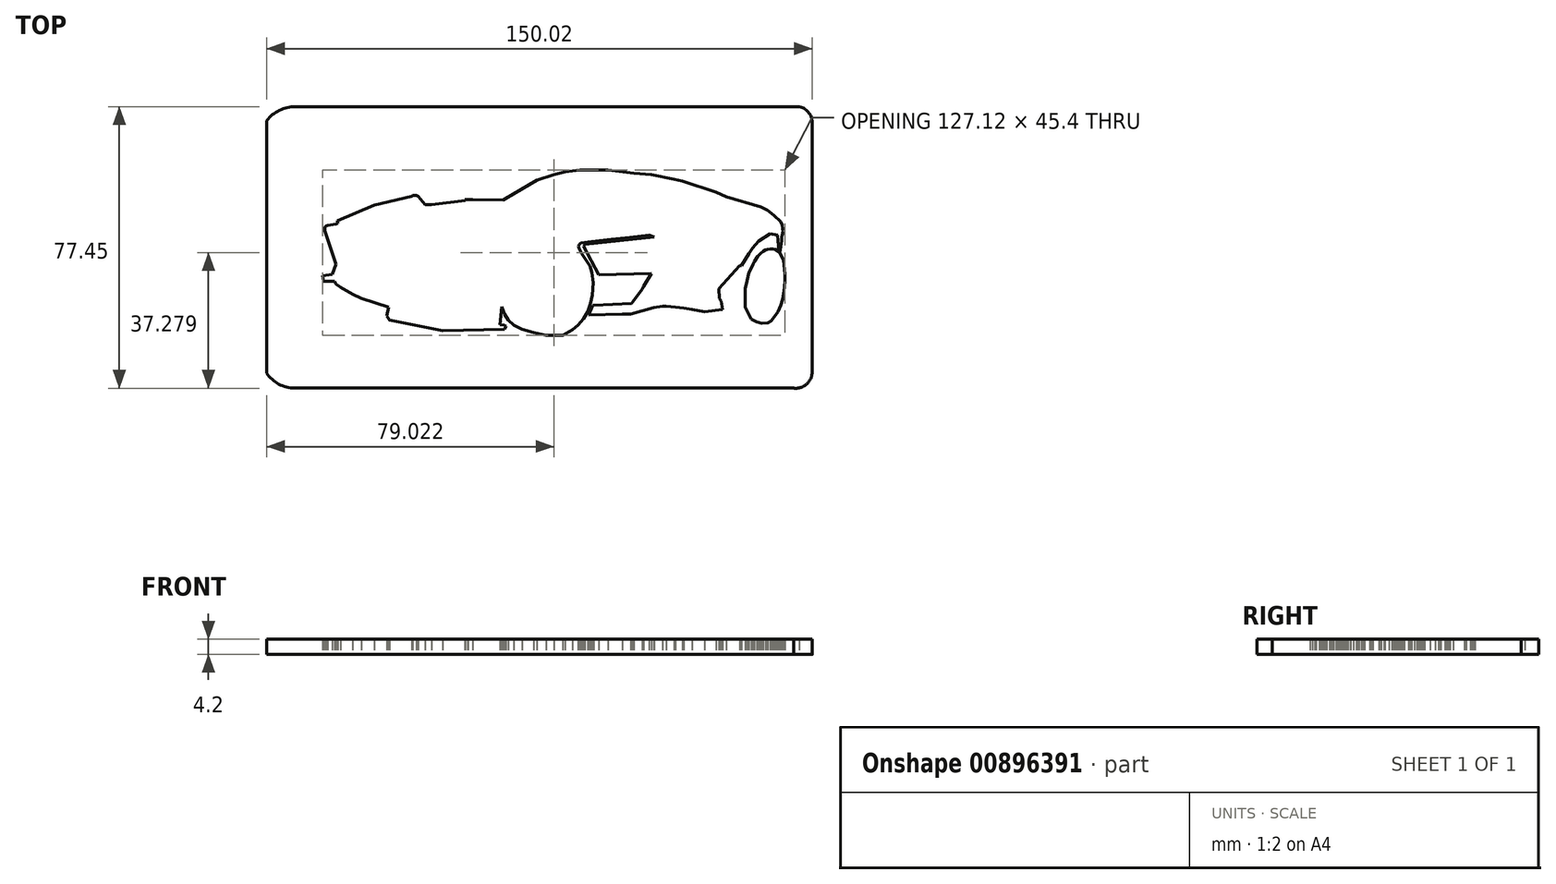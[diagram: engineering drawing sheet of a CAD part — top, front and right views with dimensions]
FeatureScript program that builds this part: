
annotation { "Feature Type Name" : "Feature", "Feature Type Description" : "" }
export const myFeature = defineFeature(function(context is Context, id is Id, definition is map)
    precondition{}
    {
        {
            var Q0;
            Q0=qCreatedBy(makeId("Top.planeOp"),FACE);
            var sketch = newSketch(context, id + "F0", { "sketchPlane" : qUnion([Q0])});
            skLineSegment(sketch, "E0", {"start": v(46.02, 12.97) * mm, "end": v(46.33, 10.6) * mm});
            skLineSegment(sketch, "E1", {"start": v(46.33, 10.6) * mm, "end": v(41.36, 9.95) * mm});
            skLineSegment(sketch, "E2", {"start": v(41.36, 9.95) * mm, "end": v(37.93, 10.6) * mm});
            skLineSegment(sketch, "E3", {"start": v(37.93, 10.6) * mm, "end": v(35.73, 10.96) * mm});
            skLineSegment(sketch, "E4", {"start": v(35.73, 10.96) * mm, "end": v(33.38, 11.3) * mm});
            skLineSegment(sketch, "E5", {"start": v(33.38, 11.3) * mm, "end": v(30.83, 11.58) * mm});
            skLineSegment(sketch, "E6", {"start": v(30.83, 11.58) * mm, "end": v(29.85, 11.58) * mm});
            skLineSegment(sketch, "E7", {"start": v(29.85, 11.58) * mm, "end": v(27.45, 11.2) * mm});
            skLineSegment(sketch, "E8", {"start": v(27.45, 11.2) * mm, "end": v(23.97, 10.17) * mm});
            skLineSegment(sketch, "E9", {"start": v(23.97, 10.17) * mm, "end": v(21.11, 9.32) * mm});
            skLineSegment(sketch, "E10", {"start": v(21.11, 9.32) * mm, "end": v(18.74, 9.32) * mm});
            skLineSegment(sketch, "E11", {"start": v(18.74, 9.32) * mm, "end": v(9.48, 9.1) * mm});
            skLineSegment(sketch, "E12", {"start": v(17.88, 9.3) * mm, "end": v(21.5, 10.48) * mm});
            skLineSegment(sketch, "E13", {"start": v(21.5, 10.48) * mm, "end": v(24.88, 11.32) * mm});
            skLineSegment(sketch, "E14", {"start": v(24.88, 11.32) * mm, "end": v(28.43, 12.23) * mm});
            skLineSegment(sketch, "E15", {"start": v(28.43, 12.23) * mm, "end": v(29.17, 12.25) * mm});
            skLineSegment(sketch, "E16", {"start": v(29.17, 12.25) * mm, "end": v(28.65, 11.39) * mm});
            skLineSegment(sketch, "E17", {"start": v(28.65, 11.39) * mm, "end": v(29.17, 12.25) * mm});
            skLineSegment(sketch, "E18", {"start": v(32.87, 12.25) * mm, "end": v(29.17, 12.25) * mm});
            skLineSegment(sketch, "E19", {"start": v(32.87, 12.25) * mm, "end": v(40.8, 12.42) * mm});
            skLineSegment(sketch, "E20", {"start": v(40.8, 12.42) * mm, "end": v(46.02, 12.97) * mm});
            skLineSegment(sketch, "E21", {"start": v(46.02, 12.97) * mm, "end": v(45.52, 13.64) * mm});
            skLineSegment(sketch, "E22", {"start": v(45.52, 13.64) * mm, "end": v(41.32, 13.38) * mm});
            skLineSegment(sketch, "E23", {"start": v(41.32, 13.38) * mm, "end": v(31.91, 13.38) * mm});
            skLineSegment(sketch, "E24", {"start": v(31.91, 13.38) * mm, "end": v(28.26, 13) * mm});
            skLineSegment(sketch, "E25", {"start": v(28.26, 13) * mm, "end": v(21.76, 12.85) * mm});
            skLineSegment(sketch, "E26", {"start": v(21.76, 12.85) * mm, "end": v(21.38, 12.23) * mm});
            skLineSegment(sketch, "E27", {"start": v(21.38, 12.23) * mm, "end": v(21.7, 11.82) * mm});
            skLineSegment(sketch, "E28", {"start": v(21.7, 11.82) * mm, "end": v(28.43, 12.23) * mm});
            skLineSegment(sketch, "E29", {"start": v(21.7, 11.82) * mm, "end": v(21.93, 11.15) * mm});
            skLineSegment(sketch, "E30", {"start": v(21.93, 11.15) * mm, "end": v(13.63, 10.86) * mm});
            skLineSegment(sketch, "E31", {"start": v(13.63, 10.86) * mm, "end": v(10.15, 10.65) * mm});
            skLineSegment(sketch, "E32", {"start": v(10.15, 10.65) * mm, "end": v(9.48, 9.1) * mm});
            skLineSegment(sketch, "E33", {"start": v(10.15, 10.65) * mm, "end": v(10.66, 11.82) * mm});
            skLineSegment(sketch, "E34", {"start": v(10.9, 11.82) * mm, "end": v(21.38, 12.23) * mm});
            skLineSegment(sketch, "E35", {"start": v(21.76, 12.85) * mm, "end": v(24.3, 16.21) * mm});
            skLineSegment(sketch, "E36", {"start": v(24.3, 16.21) * mm, "end": v(38.2, 18.23) * mm});
            skLineSegment(sketch, "E37", {"start": v(38.2, 18.23) * mm, "end": v(43.88, 22) * mm});
            skLineSegment(sketch, "E38", {"start": v(43.88, 22) * mm, "end": v(42.33, 23.24) * mm});
            skLineSegment(sketch, "E39", {"start": v(42.33, 23.24) * mm, "end": v(47.12, 23.24) * mm});
            skLineSegment(sketch, "E40", {"start": v(47.12, 23.24) * mm, "end": v(49.9, 22.62) * mm});
            skLineSegment(sketch, "E41", {"start": v(49.9, 22.62) * mm, "end": v(43.88, 22) * mm});
            skLineSegment(sketch, "E42", {"start": v(49.9, 22.62) * mm, "end": v(44.7, 16.76) * mm});
            skLineSegment(sketch, "E43", {"start": v(44.7, 16.76) * mm, "end": v(44.7, 14.03) * mm});
            skLineSegment(sketch, "E44", {"start": v(44.7, 14.03) * mm, "end": v(44.98, 13.61) * mm});
            skLineSegment(sketch, "E45", {"start": v(44.98, 13.61) * mm, "end": v(45.52, 13.64) * mm});
            skLineSegment(sketch, "E46", {"start": v(45.52, 13.64) * mm, "end": v(45.34, 16.38) * mm});
            skLineSegment(sketch, "E47", {"start": v(45.34, 16.38) * mm, "end": v(51.01, 22.67) * mm});
            skLineSegment(sketch, "E48", {"start": v(51.01, 22.67) * mm, "end": v(51.56, 22.7) * mm});
            skLineSegment(sketch, "E49", {"start": v(51.56, 22.7) * mm, "end": v(51.01, 22.67) * mm});
            skLineSegment(sketch, "E50", {"start": v(51.56, 22.7) * mm, "end": v(53.55, 26.02) * mm});
            skLineSegment(sketch, "E51", {"start": v(53.55, 26.02) * mm, "end": v(54.56, 27.48) * mm});
            skLineSegment(sketch, "E52", {"start": v(54.56, 27.48) * mm, "end": v(56.31, 29.42) * mm});
            skLineSegment(sketch, "E53", {"start": v(56.31, 29.42) * mm, "end": v(57.68, 30.33) * mm});
            skLineSegment(sketch, "E54", {"start": v(57.68, 30.33) * mm, "end": v(59.45, 31.5) * mm});
            skLineSegment(sketch, "E55", {"start": v(59.45, 31.5) * mm, "end": v(61.43, 31.05) * mm});
            skLineSegment(sketch, "E56", {"start": v(61.43, 31.05) * mm, "end": v(61.89, 26.5) * mm});
            skLineSegment(sketch, "E57", {"start": v(61.89, 26.5) * mm, "end": v(62.16, 26.26) * mm});
            skLineSegment(sketch, "E58", {"start": v(62.16, 26.26) * mm, "end": v(62.56, 29.5) * mm});
            skLineSegment(sketch, "E59", {"start": v(62.56, 29.5) * mm, "end": v(62.56, 30.7) * mm});
            skLineSegment(sketch, "E60", {"start": v(62.56, 30.7) * mm, "end": v(62.76, 30.92) * mm});
            skLineSegment(sketch, "E61", {"start": v(62.76, 30.92) * mm, "end": v(62.88, 31.47) * mm});
            skLineSegment(sketch, "E62", {"start": v(62.88, 31.47) * mm, "end": v(63.06, 32.25) * mm});
            skLineSegment(sketch, "E63", {"start": v(63.06, 32.25) * mm, "end": v(62.88, 32.9) * mm});
            skLineSegment(sketch, "E64", {"start": v(62.88, 32.9) * mm, "end": v(62.74, 33.85) * mm});
            skLineSegment(sketch, "E65", {"start": v(62.74, 33.85) * mm, "end": v(62.4, 34.82) * mm});
            skLineSegment(sketch, "E66", {"start": v(62.4, 34.82) * mm, "end": v(60.48, 36.55) * mm});
            skLineSegment(sketch, "E67", {"start": v(60.48, 36.55) * mm, "end": v(57.7, 36.88) * mm});
            skLineSegment(sketch, "E68", {"start": v(57.7, 36.88) * mm, "end": v(56.06, 36.64) * mm});
            skLineSegment(sketch, "E69", {"start": v(56.06, 36.64) * mm, "end": v(53.85, 35.63) * mm});
            skLineSegment(sketch, "E70", {"start": v(53.85, 35.63) * mm, "end": v(49.63, 33.21) * mm});
            skLineSegment(sketch, "E71", {"start": v(49.63, 33.21) * mm, "end": v(47.78, 32.6) * mm});
            skLineSegment(sketch, "E72", {"start": v(47.78, 32.6) * mm, "end": v(44.93, 31.94) * mm});
            skLineSegment(sketch, "E73", {"start": v(44.93, 31.94) * mm, "end": v(43.07, 31.67) * mm});
            skLineSegment(sketch, "E74", {"start": v(43.07, 31.67) * mm, "end": v(39.45, 31.67) * mm});
            skLineSegment(sketch, "E75", {"start": v(39.45, 31.67) * mm, "end": v(35.8, 32.26) * mm});
            skLineSegment(sketch, "E76", {"start": v(35.8, 32.26) * mm, "end": v(35.02, 32.15) * mm});
            skLineSegment(sketch, "E77", {"start": v(35.02, 32.15) * mm, "end": v(35.43, 31.78) * mm});
            skLineSegment(sketch, "E78", {"start": v(35.43, 31.78) * mm, "end": v(34.34, 31.05) * mm});
            skLineSegment(sketch, "E79", {"start": v(34.34, 31.05) * mm, "end": v(36.34, 29.93) * mm});
            skLineSegment(sketch, "E80", {"start": v(36.34, 29.93) * mm, "end": v(37.89, 28.53) * mm});
            skLineSegment(sketch, "E81", {"start": v(37.89, 28.53) * mm, "end": v(39.87, 26.75) * mm});
            skLineSegment(sketch, "E82", {"start": v(39.87, 26.75) * mm, "end": v(42.33, 23.24) * mm});
            skLineSegment(sketch, "E83", {"start": v(47.12, 23.24) * mm, "end": v(49.28, 26.26) * mm});
            skLineSegment(sketch, "E84", {"start": v(49.28, 26.26) * mm, "end": v(52.77, 30.14) * mm});
            skLineSegment(sketch, "E85", {"start": v(52.77, 30.14) * mm, "end": v(55.72, 32.9) * mm});
            skLineSegment(sketch, "E86", {"start": v(55.72, 32.9) * mm, "end": v(57.45, 34.05) * mm});
            skLineSegment(sketch, "E87", {"start": v(57.45, 34.05) * mm, "end": v(58.82, 34.25) * mm});
            skLineSegment(sketch, "E88", {"start": v(58.82, 34.25) * mm, "end": v(60.58, 33.85) * mm});
            skLineSegment(sketch, "E89", {"start": v(60.58, 33.85) * mm, "end": v(61.4, 33.29) * mm});
            skLineSegment(sketch, "E90", {"start": v(61.88, 32.5) * mm, "end": v(62.56, 30.7) * mm});
            skLineSegment(sketch, "E91", {"start": v(61.4, 33.29) * mm, "end": v(61.88, 32.5) * mm});
            skLineSegment(sketch, "E92", {"start": v(41.01, 26.8) * mm, "end": v(42.38, 27.92) * mm});
            skLineSegment(sketch, "E93", {"start": v(42.38, 27.92) * mm, "end": v(43.42, 29.13) * mm});
            skLineSegment(sketch, "E94", {"start": v(43.42, 29.13) * mm, "end": v(44.8, 30.3) * mm});
            skLineSegment(sketch, "E95", {"start": v(24.3, 16.21) * mm, "end": v(24.83, 16.95) * mm});
            skLineSegment(sketch, "E96", {"start": v(24.83, 16.95) * mm, "end": v(27.35, 17.42) * mm});
            skLineSegment(sketch, "E97", {"start": v(27.35, 17.42) * mm, "end": v(28.1, 17.53) * mm});
            skLineSegment(sketch, "E98", {"start": v(28.1, 17.53) * mm, "end": v(28.43, 17.58) * mm});
            skLineSegment(sketch, "E99", {"start": v(28.43, 17.58) * mm, "end": v(37, 18.72) * mm});
            skLineSegment(sketch, "E100", {"start": v(37, 18.72) * mm, "end": v(34.58, 21.2) * mm});
            skLineSegment(sketch, "E101", {"start": v(34.58, 21.2) * mm, "end": v(34.24, 21.16) * mm});
            skLineSegment(sketch, "E102", {"start": v(34.24, 21.16) * mm, "end": v(26.6, 20.2) * mm});
            skLineSegment(sketch, "E103", {"start": v(26.6, 20.2) * mm, "end": v(24.65, 16.95) * mm});
            skLineSegment(sketch, "E104", {"start": v(24.65, 16.95) * mm, "end": v(24.3, 16.21) * mm});
            skLineSegment(sketch, "E105", {"start": v(24.83, 16.95) * mm, "end": v(24.65, 16.95) * mm});
            skLineSegment(sketch, "E106", {"start": v(25.36, 17.89) * mm, "end": v(36.32, 19.41) * mm});
            skLineSegment(sketch, "E107", {"start": v(35.79, 19.96) * mm, "end": v(25.75, 18.77) * mm});
            skLineSegment(sketch, "E108", {"start": v(25.36, 17.89) * mm, "end": v(25.22, 17.89) * mm});
            skLineSegment(sketch, "E109", {"start": v(26.1, 19.37) * mm, "end": v(35.19, 20.58) * mm});
            skLineSegment(sketch, "E110", {"start": v(34.58, 21.2) * mm, "end": v(37.15, 22.86) * mm});
            skLineSegment(sketch, "E111", {"start": v(35.19, 20.58) * mm, "end": v(38.93, 22.8) * mm});
            skLineSegment(sketch, "E112", {"start": v(35.79, 19.96) * mm, "end": v(40.07, 22.47) * mm});
            skLineSegment(sketch, "E113", {"start": v(36.32, 19.41) * mm, "end": v(39.35, 21.2) * mm});
            skLineSegment(sketch, "E114", {"start": v(37, 18.72) * mm, "end": v(41.95, 22.94) * mm});
            skLineSegment(sketch, "E115", {"start": v(41.95, 22.94) * mm, "end": v(39.54, 26.32) * mm});
            skLineSegment(sketch, "E116", {"start": v(39.54, 26.32) * mm, "end": v(38.05, 28.08) * mm});
            skLineSegment(sketch, "E117", {"start": v(38.05, 28.08) * mm, "end": v(35.94, 29.68) * mm});
            skLineSegment(sketch, "E118", {"start": v(35.94, 29.68) * mm, "end": v(33.28, 30.2) * mm});
            skLineSegment(sketch, "E119", {"start": v(33.28, 30.2) * mm, "end": v(32.31, 30.02) * mm});
            skLineSegment(sketch, "E120", {"start": v(32.31, 30.02) * mm, "end": v(31.77, 29.66) * mm});
            skLineSegment(sketch, "E121", {"start": v(31.77, 29.66) * mm, "end": v(32.15, 29.03) * mm});
            skLineSegment(sketch, "E122", {"start": v(32.15, 29.03) * mm, "end": v(33.31, 27.64) * mm});
            skLineSegment(sketch, "E123", {"start": v(33.31, 27.64) * mm, "end": v(34.28, 26.17) * mm});
            skLineSegment(sketch, "E124", {"start": v(34.28, 26.17) * mm, "end": v(36.03, 24.08) * mm});
            skLineSegment(sketch, "E125", {"start": v(36.03, 24.08) * mm, "end": v(36.1, 23.96) * mm});
            skLineSegment(sketch, "E126", {"start": v(36.1, 23.96) * mm, "end": v(37.15, 22.86) * mm});
            skLineSegment(sketch, "E127", {"start": v(37.15, 22.86) * mm, "end": v(38.93, 23.91) * mm});
            skLineSegment(sketch, "E128", {"start": v(27.56, 24.66) * mm, "end": v(34.58, 21.2) * mm});
            skLineSegment(sketch, "E129", {"start": v(26.6, 20.2) * mm, "end": v(26.83, 20.58) * mm});
            skLineSegment(sketch, "E130", {"start": v(26.83, 20.58) * mm, "end": v(27.92, 30.03) * mm});
            skLineSegment(sketch, "E131", {"start": v(27.92, 30.03) * mm, "end": v(27.56, 30.59) * mm});
            skLineSegment(sketch, "E132", {"start": v(27.56, 30.59) * mm, "end": v(8.52, 28.58) * mm});
            skLineSegment(sketch, "E133", {"start": v(8.52, 28.58) * mm, "end": v(8.12, 28.06) * mm});
            skLineSegment(sketch, "E134", {"start": v(8.12, 28.06) * mm, "end": v(12.32, 20.1) * mm});
            skLineSegment(sketch, "E135", {"start": v(12.32, 20.1) * mm, "end": v(26.83, 20.58) * mm});
            skLineSegment(sketch, "E136", {"start": v(10.9, 11.82) * mm, "end": v(10.66, 11.82) * mm});
            skLineSegment(sketch, "E137", {"start": v(10.64, 11.82) * mm, "end": v(11.7, 15.8) * mm});
            skLineSegment(sketch, "E138", {"start": v(11.7, 15.8) * mm, "end": v(12.32, 20.1) * mm});
            skLineSegment(sketch, "E139", {"start": v(11.25, 27.9) * mm, "end": v(10.75, 26.73) * mm});
            skLineSegment(sketch, "E140", {"start": v(10.75, 26.73) * mm, "end": v(11.49, 26.02) * mm});
            skLineSegment(sketch, "E141", {"start": v(11.49, 26.02) * mm, "end": v(21.03, 27.43) * mm});
            skLineSegment(sketch, "E142", {"start": v(21.03, 27.43) * mm, "end": v(21.7, 28.48) * mm});
            skLineSegment(sketch, "E143", {"start": v(21.7, 28.48) * mm, "end": v(11.25, 27.9) * mm});
            skLineSegment(sketch, "E144", {"start": v(11.25, 27.9) * mm, "end": v(11.06, 27.99) * mm});
            skLineSegment(sketch, "E145", {"start": v(11.06, 27.99) * mm, "end": v(10.27, 26.58) * mm});
            skLineSegment(sketch, "E146", {"start": v(10.27, 26.58) * mm, "end": v(11.43, 25.77) * mm});
            skLineSegment(sketch, "E147", {"start": v(11.43, 25.77) * mm, "end": v(11.49, 26.02) * mm});
            skLineSegment(sketch, "E148", {"start": v(11.43, 25.77) * mm, "end": v(17.72, 26.94) * mm});
            skLineSegment(sketch, "E149", {"start": v(11.06, 27.99) * mm, "end": v(16.78, 28.2) * mm});
            skLineSegment(sketch, "E150", {"start": v(7.66, 25.99) * mm, "end": v(6.92, 27.49) * mm});
            skLineSegment(sketch, "E151", {"start": v(6.92, 27.49) * mm, "end": v(6.8, 27.98) * mm});
            skLineSegment(sketch, "E152", {"start": v(6.8, 27.98) * mm, "end": v(6.96, 28.5) * mm});
            skLineSegment(sketch, "E153", {"start": v(6.96, 28.5) * mm, "end": v(7.36, 28.92) * mm});
            skLineSegment(sketch, "E154", {"start": v(7.36, 28.92) * mm, "end": v(10.36, 29.33) * mm});
            skLineSegment(sketch, "E155", {"start": v(10.36, 29.33) * mm, "end": v(15.7, 29.9) * mm});
            skLineSegment(sketch, "E156", {"start": v(15.7, 29.9) * mm, "end": v(20.77, 30.46) * mm});
            skLineSegment(sketch, "E157", {"start": v(20.77, 30.46) * mm, "end": v(26.13, 31.02) * mm});
            skLineSegment(sketch, "E158", {"start": v(26.13, 31.02) * mm, "end": v(27.56, 30.59) * mm});
            skLineSegment(sketch, "E159", {"start": v(10.66, 11.82) * mm, "end": v(9.97, 11.82) * mm});
            skLineSegment(sketch, "E160", {"start": v(15.7, 29.9) * mm, "end": v(15.33, 30.17) * mm});
            skLineSegment(sketch, "E161", {"start": v(15.33, 30.54) * mm, "end": v(15.33, 30.17) * mm});
            skLineSegment(sketch, "E162", {"start": v(15.33, 30.54) * mm, "end": v(15.06, 30.7) * mm});
            skLineSegment(sketch, "E163", {"start": v(15.06, 30.7) * mm, "end": v(14.87, 31.08) * mm});
            skLineSegment(sketch, "E164", {"start": v(14.87, 31.08) * mm, "end": v(14.5, 31.04) * mm});
            skLineSegment(sketch, "E165", {"start": v(14.5, 31.04) * mm, "end": v(14.3, 30.94) * mm});
            skLineSegment(sketch, "E166", {"start": v(14.3, 30.94) * mm, "end": v(8.21, 29.9) * mm});
            skLineSegment(sketch, "E167", {"start": v(13.1, 30.74) * mm, "end": v(12.9, 31.1) * mm});
            skLineSegment(sketch, "E168", {"start": v(12.9, 31.1) * mm, "end": v(12.9, 32.83) * mm});
            skLineSegment(sketch, "E169", {"start": v(12.9, 32.83) * mm, "end": v(12.53, 33.2) * mm});
            skLineSegment(sketch, "E170", {"start": v(12.53, 33.2) * mm, "end": v(4.45, 31.8) * mm});
            skLineSegment(sketch, "E171", {"start": v(4.45, 31.8) * mm, "end": v(7.43, 29.44) * mm});
            skLineSegment(sketch, "E172", {"start": v(7.43, 29.44) * mm, "end": v(6.8, 29.01) * mm});
            skLineSegment(sketch, "E173", {"start": v(6.8, 29.01) * mm, "end": v(6.33, 28.35) * mm});
            skLineSegment(sketch, "E174", {"start": v(6.33, 28.35) * mm, "end": v(6.33, 27.84) * mm});
            skLineSegment(sketch, "E175", {"start": v(6.33, 27.84) * mm, "end": v(6.57, 27.31) * mm});
            skLineSegment(sketch, "E176", {"start": v(6.57, 27.31) * mm, "end": v(7.1, 26.46) * mm});
            skLineSegment(sketch, "E177", {"start": v(7.1, 26.46) * mm, "end": v(7.66, 25.99) * mm});
            skLineSegment(sketch, "E178", {"start": v(15.06, 30.7) * mm, "end": v(11.3, 29.7) * mm});
            skLineSegment(sketch, "E179", {"start": v(12.81, 32.92) * mm, "end": v(7.38, 31.3) * mm});
            skLineSegment(sketch, "E180", {"start": v(7.38, 31.3) * mm, "end": v(12.9, 31.1) * mm});
            skLineSegment(sketch, "E181", {"start": v(6.33, 28.35) * mm, "end": v(5.03, 29.64) * mm});
            skLineSegment(sketch, "E182", {"start": v(5.03, 29.64) * mm, "end": v(4.82, 27.98) * mm});
            skLineSegment(sketch, "E183", {"start": v(5.03, 29.64) * mm, "end": v(2.75, 31.92) * mm});
            skLineSegment(sketch, "E184", {"start": v(2.75, 31.92) * mm, "end": v(2.42, 32.67) * mm});
            skLineSegment(sketch, "E185", {"start": v(2.42, 32.67) * mm, "end": v(2.08, 32.52) * mm});
            skLineSegment(sketch, "E186", {"start": v(2.08, 32.52) * mm, "end": v(1.85, 32.75) * mm});
            skLineSegment(sketch, "E187", {"start": v(1.85, 32.75) * mm, "end": v(1.16, 33.06) * mm});
            skLineSegment(sketch, "E188", {"start": v(1.16, 33.06) * mm, "end": v(-1.02, 33.82) * mm});
            skLineSegment(sketch, "E189", {"start": v(-1.02, 33.82) * mm, "end": v(1.56, 34) * mm});
            skLineSegment(sketch, "E190", {"start": v(1.56, 34) * mm, "end": v(4.45, 31.8) * mm});
            skLineSegment(sketch, "E191", {"start": v(1.56, 34) * mm, "end": v(1.56, 32.88) * mm});
            skLineSegment(sketch, "E192", {"start": v(1.56, 34) * mm, "end": v(1.77, 34.27) * mm});
            skLineSegment(sketch, "E193", {"start": v(1.77, 34.27) * mm, "end": v(7.95, 34.96) * mm});
            skLineSegment(sketch, "E194", {"start": v(7.95, 34.96) * mm, "end": v(10.49, 32.84) * mm});
            skLineSegment(sketch, "E195", {"start": v(2.75, 31.92) * mm, "end": v(2.6, 31.6) * mm});
            skLineSegment(sketch, "E196", {"start": v(2.6, 31.6) * mm, "end": v(3.02, 30.82) * mm});
            skLineSegment(sketch, "E197", {"start": v(3.03, 30.77) * mm, "end": v(1.23, 30.16) * mm});
            skLineSegment(sketch, "E198", {"start": v(1.23, 30.16) * mm, "end": v(1.23, 31.03) * mm});
            skLineSegment(sketch, "E199", {"start": v(1.23, 31.03) * mm, "end": v(1.39, 31.17) * mm});
            skLineSegment(sketch, "E200", {"start": v(1.39, 31.17) * mm, "end": v(2.6, 31.6) * mm});
            skLineSegment(sketch, "E201", {"start": v(2.75, 31.92) * mm, "end": v(1.23, 31.6) * mm});
            skPoint(sketch, "E201.endSnap0", {"position": v(1.23, 30.6) * mm});
            skLineSegment(sketch, "E202", {"start": v(1.23, 31.6) * mm, "end": v(1.09, 31.03) * mm});
            skLineSegment(sketch, "E203", {"start": v(1.09, 31.03) * mm, "end": v(1.09, 30.16) * mm});
            skLineSegment(sketch, "E204", {"start": v(1.09, 30.16) * mm, "end": v(-1.84, 29.3) * mm});
            skLineSegment(sketch, "E205", {"start": v(-1.84, 29.3) * mm, "end": v(-3.52, 28.53) * mm});
            skLineSegment(sketch, "E206", {"start": v(-3.52, 28.53) * mm, "end": v(-4.85, 27.84) * mm});
            skLineSegment(sketch, "E207", {"start": v(-4.85, 27.84) * mm, "end": v(-5.64, 27.19) * mm});
            skLineSegment(sketch, "E208", {"start": v(-5.64, 27.19) * mm, "end": v(-6.73, 26.3) * mm});
            skLineSegment(sketch, "E209", {"start": v(-6.73, 26.3) * mm, "end": v(-5.83, 27.19) * mm});
            skLineSegment(sketch, "E210", {"start": v(-5.83, 27.19) * mm, "end": v(-4.92, 27.92) * mm});
            skLineSegment(sketch, "E211", {"start": v(-4.92, 27.92) * mm, "end": v(-3.65, 28.58) * mm});
            skLineSegment(sketch, "E212", {"start": v(-3.65, 28.58) * mm, "end": v(-1.84, 29.3) * mm});
            skLineSegment(sketch, "E213", {"start": v(1.85, 32.52) * mm, "end": v(0.7, 32.25) * mm});
            skLineSegment(sketch, "E214", {"start": v(0.7, 32.25) * mm, "end": v(0.3, 30.83) * mm});
            skLineSegment(sketch, "E215", {"start": v(0.3, 30.83) * mm, "end": v(-0.13, 30.83) * mm});
            skLineSegment(sketch, "E216", {"start": v(-0.13, 30.83) * mm, "end": v(0.17, 32.05) * mm});
            skLineSegment(sketch, "E217", {"start": v(0.17, 32.05) * mm, "end": v(0.7, 32.25) * mm});
            skLineSegment(sketch, "E218", {"start": v(-0.13, 30.83) * mm, "end": v(-2.4, 30.02) * mm});
            skLineSegment(sketch, "E219", {"start": v(-2.4, 30.02) * mm, "end": v(-4.08, 29.43) * mm});
            skLineSegment(sketch, "E220", {"start": v(-4.08, 29.43) * mm, "end": v(-5.07, 28.98) * mm});
            skLineSegment(sketch, "E221", {"start": v(-5.07, 28.98) * mm, "end": v(-6.76, 27.85) * mm});
            skLineSegment(sketch, "E222", {"start": v(-6.76, 27.85) * mm, "end": v(-7.88, 26.73) * mm});
            skLineSegment(sketch, "E223", {"start": v(-7.88, 26.73) * mm, "end": v(-9.98, 23.95) * mm});
            skLineSegment(sketch, "E224", {"start": v(-9.98, 23.95) * mm, "end": v(-11.7, 21.06) * mm});
            skLineSegment(sketch, "E225", {"start": v(-11.7, 21.06) * mm, "end": v(-14.23, 16.13) * mm});
            skLineSegment(sketch, "E226", {"start": v(-14.23, 16.13) * mm, "end": v(-16.25, 11.5) * mm});
            skLineSegment(sketch, "E227", {"start": v(-16.25, 11.5) * mm, "end": v(-16.25, 11.04) * mm});
            skLineSegment(sketch, "E228", {"start": v(-16.25, 11.04) * mm, "end": v(-14.32, 11.37) * mm});
            skLineSegment(sketch, "E229", {"start": v(-14.32, 11.37) * mm, "end": v(-14.82, 6.38) * mm});
            skLineSegment(sketch, "E230", {"start": v(-14.82, 6.38) * mm, "end": v(-13.63, 6.26) * mm});
            skLineSegment(sketch, "E231", {"start": v(-13.63, 6.26) * mm, "end": v(-13.2, 6.07) * mm});
            skLineSegment(sketch, "E232", {"start": v(-13.2, 6.07) * mm, "end": v(-13.6, 5.14) * mm});
            skLineSegment(sketch, "E233", {"start": v(-13.6, 5.14) * mm, "end": v(-30.55, 4.76) * mm});
            skLineSegment(sketch, "E234", {"start": v(-30.55, 4.76) * mm, "end": v(-31.58, 5.78) * mm});
            skLineSegment(sketch, "E235", {"start": v(-31.07, 5.27) * mm, "end": v(-13.37, 5.66) * mm});
            skLineSegment(sketch, "E236", {"start": v(-14.82, 6.38) * mm, "end": v(-27.36, 6) * mm});
            skLineSegment(sketch, "E237", {"start": v(-27.36, 6) * mm, "end": v(-25.98, 9.2) * mm});
            skLineSegment(sketch, "E238", {"start": v(-25.98, 9.2) * mm, "end": v(-16.25, 11.04) * mm});
            skLineSegment(sketch, "E239", {"start": v(-16.25, 11.5) * mm, "end": v(-26.4, 9.57) * mm});
            skLineSegment(sketch, "E240", {"start": v(-26.4, 9.57) * mm, "end": v(-28.65, 6.38) * mm});
            skLineSegment(sketch, "E241", {"start": v(-28.65, 6.38) * mm, "end": v(-27.36, 6) * mm});
            skLineSegment(sketch, "E242", {"start": v(-28.23, 6.98) * mm, "end": v(-30.43, 6.93) * mm});
            skLineSegment(sketch, "E243", {"start": v(-30.43, 6.93) * mm, "end": v(-31.14, 6.8) * mm});
            skLineSegment(sketch, "E244", {"start": v(-31.14, 6.8) * mm, "end": v(-32.86, 7.3) * mm});
            skLineSegment(sketch, "E245", {"start": v(-30.55, 4.76) * mm, "end": v(-45.21, 7.67) * mm});
            skLineSegment(sketch, "E246", {"start": v(-45.21, 7.67) * mm, "end": v(-45.95, 8.88) * mm});
            skLineSegment(sketch, "E247", {"start": v(-45.95, 8.88) * mm, "end": v(-45.41, 11.24) * mm});
            skLineSegment(sketch, "E248", {"start": v(-45.95, 8.88) * mm, "end": v(-31.58, 5.78) * mm});
            skLineSegment(sketch, "E249", {"start": v(-45.95, 8.88) * mm, "end": v(-42.57, 9.23) * mm});
            skLineSegment(sketch, "E250", {"start": v(-42.57, 9.23) * mm, "end": v(-37.9, 8.16) * mm});
            skLineSegment(sketch, "E251", {"start": v(-37.9, 8.16) * mm, "end": v(-39.32, 7.45) * mm});
            skLineSegment(sketch, "E252", {"start": v(-37.9, 8.16) * mm, "end": v(-36.33, 8.6) * mm});
            skLineSegment(sketch, "E253", {"start": v(-36.33, 8.6) * mm, "end": v(-34.7, 9.35) * mm});
            skLineSegment(sketch, "E254", {"start": v(-34.7, 9.35) * mm, "end": v(-32.06, 11.73) * mm});
            skLineSegment(sketch, "E255", {"start": v(-32.06, 11.73) * mm, "end": v(-31.22, 11.73) * mm});
            skLineSegment(sketch, "E256", {"start": v(-31.22, 11.73) * mm, "end": v(-32.63, 10) * mm});
            skLineSegment(sketch, "E257", {"start": v(-32.63, 10) * mm, "end": v(-33.08, 9.49) * mm});
            skLineSegment(sketch, "E258", {"start": v(-33.08, 9.49) * mm, "end": v(-34.08, 8.85) * mm});
            skLineSegment(sketch, "E259", {"start": v(-34.08, 8.85) * mm, "end": v(-35.85, 7.92) * mm});
            skLineSegment(sketch, "E260", {"start": v(-35.85, 7.92) * mm, "end": v(-36.4, 7.63) * mm});
            skLineSegment(sketch, "E261", {"start": v(-36.4, 7.63) * mm, "end": v(-34.9, 7.63) * mm});
            skLineSegment(sketch, "E262", {"start": v(-34.9, 7.63) * mm, "end": v(-36.83, 7.27) * mm});
            skLineSegment(sketch, "E263", {"start": v(-36.83, 7.27) * mm, "end": v(-34.25, 7.46) * mm});
            skLineSegment(sketch, "E264", {"start": v(-34.25, 7.46) * mm, "end": v(-32.86, 7.3) * mm});
            skLineSegment(sketch, "E265", {"start": v(-31.22, 11.73) * mm, "end": v(-30.18, 11.93) * mm});
            skLineSegment(sketch, "E266", {"start": v(-32.06, 11.73) * mm, "end": v(-44.88, 15.57) * mm});
            skLineSegment(sketch, "E267", {"start": v(-44.88, 15.57) * mm, "end": v(-49.46, 20.72) * mm});
            skLineSegment(sketch, "E268", {"start": v(-49.46, 20.72) * mm, "end": v(-50.22, 20.72) * mm});
            skLineSegment(sketch, "E269", {"start": v(-50.22, 20.72) * mm, "end": v(-50.7, 20.72) * mm});
            skLineSegment(sketch, "E270", {"start": v(-50.7, 20.72) * mm, "end": v(-53.17, 18.65) * mm});
            skLineSegment(sketch, "E271", {"start": v(-50.94, 20.25) * mm, "end": v(-50.54, 20.25) * mm});
            skLineSegment(sketch, "E272", {"start": v(-50.54, 20.25) * mm, "end": v(-51.26, 20.25) * mm});
            skLineSegment(sketch, "E273", {"start": v(-51.26, 20.25) * mm, "end": v(-50.94, 20.25) * mm});
            skLineSegment(sketch, "E274", {"start": v(-50.54, 20.25) * mm, "end": v(-45.9, 15.26) * mm});
            skLineSegment(sketch, "E275", {"start": v(-45.9, 15.26) * mm, "end": v(-32.88, 11) * mm});
            skLineSegment(sketch, "E276", {"start": v(-34.7, 12.52) * mm, "end": v(-44.02, 23.5) * mm});
            skLineSegment(sketch, "E277", {"start": v(-44.02, 23.5) * mm, "end": v(-52.98, 25.26) * mm});
            skLineSegment(sketch, "E278", {"start": v(-52.98, 25.26) * mm, "end": v(-53.91, 27.53) * mm});
            skLineSegment(sketch, "E279", {"start": v(-53.91, 27.53) * mm, "end": v(-58.62, 30.93) * mm});
            skLineSegment(sketch, "E280", {"start": v(-58.62, 30.93) * mm, "end": v(-58.48, 32.14) * mm});
            skLineSegment(sketch, "E281", {"start": v(-58.48, 32.14) * mm, "end": v(-57.8, 32.98) * mm});
            skLineSegment(sketch, "E282", {"start": v(-57.8, 32.98) * mm, "end": v(-59.01, 34.55) * mm});
            skLineSegment(sketch, "E283", {"start": v(-59.01, 34.55) * mm, "end": v(-59.38, 33.32) * mm});
            skLineSegment(sketch, "E284", {"start": v(-59.38, 33.32) * mm, "end": v(-58.48, 32.14) * mm});
            skLineSegment(sketch, "E285", {"start": v(-59.38, 33.32) * mm, "end": v(-59.83, 33.69) * mm});
            skLineSegment(sketch, "E286", {"start": v(-59.83, 33.69) * mm, "end": v(-62.48, 33.32) * mm});
            skLineSegment(sketch, "E287", {"start": v(-59.9, 34.14) * mm, "end": v(-62.17, 33.77) * mm});
            skLineSegment(sketch, "E288", {"start": v(-62.17, 33.77) * mm, "end": v(-62.64, 33.6) * mm});
            skLineSegment(sketch, "E289", {"start": v(-62.64, 33.6) * mm, "end": v(-62.96, 33.34) * mm});
            skLineSegment(sketch, "E290", {"start": v(-62.96, 33.34) * mm, "end": v(-62.96, 32.2) * mm});
            skLineSegment(sketch, "E291", {"start": v(-62.96, 32.2) * mm, "end": v(-59.12, 20.61) * mm});
            skLineSegment(sketch, "E292", {"start": v(-59.12, 20.61) * mm, "end": v(-59.72, 20.28) * mm});
            skLineSegment(sketch, "E293", {"start": v(-59.72, 20.28) * mm, "end": v(-59.88, 20.16) * mm});
            skLineSegment(sketch, "E294", {"start": v(-59.88, 20.16) * mm, "end": v(-60.08, 19.97) * mm});
            skLineSegment(sketch, "E295", {"start": v(-60.08, 19.97) * mm, "end": v(-60.08, 19.13) * mm});
            skLineSegment(sketch, "E296", {"start": v(-60.08, 19.13) * mm, "end": v(-59.3, 18.22) * mm});
            skLineSegment(sketch, "E297", {"start": v(-59.3, 18.22) * mm, "end": v(-55.38, 15.96) * mm});
            skLineSegment(sketch, "E298", {"start": v(-55.38, 15.96) * mm, "end": v(-51.26, 20.25) * mm});
            skLineSegment(sketch, "E299", {"start": v(-54.3, 15.52) * mm, "end": v(-54.3, 15.84) * mm});
            skLineSegment(sketch, "E300", {"start": v(-54.3, 15.84) * mm, "end": v(-52.98, 18.1) * mm});
            skLineSegment(sketch, "E301", {"start": v(-54.3, 15.52) * mm, "end": v(-50.66, 14.06) * mm});
            skLineSegment(sketch, "E302", {"start": v(-50.66, 14.06) * mm, "end": v(-48.28, 13.25) * mm});
            skLineSegment(sketch, "E303", {"start": v(-48.28, 13.25) * mm, "end": v(-44.72, 12.3) * mm});
            skLineSegment(sketch, "E304", {"start": v(-44.72, 12.3) * mm, "end": v(-41.74, 11.77) * mm});
            skLineSegment(sketch, "E305", {"start": v(-41.74, 11.77) * mm, "end": v(-33.2, 10.7) * mm});
            skLineSegment(sketch, "E306", {"start": v(-33.2, 10.7) * mm, "end": v(-34.7, 9.35) * mm});
            skLineSegment(sketch, "E307", {"start": v(-34.55, 9.49) * mm, "end": v(-45.41, 11.24) * mm});
            skLineSegment(sketch, "E308", {"start": v(-45.41, 11.24) * mm, "end": v(-49.32, 12.52) * mm});
            skLineSegment(sketch, "E309", {"start": v(-49.32, 12.52) * mm, "end": v(-52.98, 13.72) * mm});
            skLineSegment(sketch, "E310", {"start": v(-52.98, 13.72) * mm, "end": v(-55.31, 14.77) * mm});
            skLineSegment(sketch, "E311", {"start": v(-55.31, 14.77) * mm, "end": v(-58.64, 16.69) * mm});
            skLineSegment(sketch, "E312", {"start": v(-58.64, 16.69) * mm, "end": v(-59.95, 17.65) * mm});
            skLineSegment(sketch, "E313", {"start": v(-59.95, 17.65) * mm, "end": v(-60.26, 18.33) * mm});
            skLineSegment(sketch, "E314", {"start": v(-60.26, 18.33) * mm, "end": v(-60.34, 18.6) * mm});
            skLineSegment(sketch, "E315", {"start": v(-60.34, 18.6) * mm, "end": v(-60.08, 19.97) * mm});
            skLineSegment(sketch, "E316", {"start": v(-59.12, 20.61) * mm, "end": v(-58.56, 20.8) * mm});
            skLineSegment(sketch, "E317", {"start": v(-58.56, 20.8) * mm, "end": v(-58.06, 20.96) * mm});
            skLineSegment(sketch, "E318", {"start": v(-58.06, 20.96) * mm, "end": v(-57.59, 21.12) * mm});
            skLineSegment(sketch, "E319", {"start": v(-57.59, 21.12) * mm, "end": v(-56.78, 20.78) * mm});
            skLineSegment(sketch, "E320", {"start": v(-56.78, 20.78) * mm, "end": v(-55.5, 19.97) * mm});
            skLineSegment(sketch, "E321", {"start": v(-55.5, 19.97) * mm, "end": v(-53.17, 18.65) * mm});
            skLineSegment(sketch, "E322", {"start": v(-58.56, 20.8) * mm, "end": v(-59.53, 24.4) * mm});
            skLineSegment(sketch, "E323", {"start": v(-59.53, 24.4) * mm, "end": v(-60.34, 29.57) * mm});
            skLineSegment(sketch, "E324", {"start": v(-60.34, 29.57) * mm, "end": v(-60.6, 30.88) * mm});
            skLineSegment(sketch, "E325", {"start": v(-60.6, 30.88) * mm, "end": v(-60.7, 31.16) * mm});
            skLineSegment(sketch, "E326", {"start": v(-60.7, 31.16) * mm, "end": v(-58.94, 31.16) * mm});
            skLineSegment(sketch, "E327", {"start": v(-58.94, 31.16) * mm, "end": v(-58.71, 30.48) * mm});
            skLineSegment(sketch, "E328", {"start": v(-58.71, 30.48) * mm, "end": v(-58.35, 30.48) * mm});
            skLineSegment(sketch, "E329", {"start": v(-58.35, 30.48) * mm, "end": v(-58.35, 30.74) * mm});
            skLineSegment(sketch, "E330", {"start": v(-58.94, 31.16) * mm, "end": v(-58.93, 32.73) * mm});
            skLineSegment(sketch, "E331", {"start": v(-58.35, 30.48) * mm, "end": v(-57.6, 27.8) * mm});
            skLineSegment(sketch, "E332", {"start": v(-57.6, 27.8) * mm, "end": v(-60.6, 30.88) * mm});
            skLineSegment(sketch, "E333", {"start": v(-60.6, 30.88) * mm, "end": v(-58.5, 27.85) * mm});
            skLineSegment(sketch, "E334", {"start": v(-58.5, 27.85) * mm, "end": v(-56.5, 25.79) * mm});
            skLineSegment(sketch, "E335", {"start": v(-56.5, 25.79) * mm, "end": v(-55.69, 21.88) * mm});
            skLineSegment(sketch, "E336", {"start": v(-55.69, 21.88) * mm, "end": v(-56.93, 23.82) * mm});
            skLineSegment(sketch, "E337", {"start": v(-56.93, 23.82) * mm, "end": v(-55.65, 21.43) * mm});
            skLineSegment(sketch, "E338", {"start": v(-55.65, 21.43) * mm, "end": v(-55.5, 21.58) * mm});
            skLineSegment(sketch, "E339", {"start": v(-55.5, 21.58) * mm, "end": v(-55.69, 21.88) * mm});
            skLineSegment(sketch, "E340", {"start": v(-55.99, 22.05) * mm, "end": v(-57.15, 22.05) * mm});
            skLineSegment(sketch, "E341", {"start": v(-57.15, 22.05) * mm, "end": v(-58.03, 21.28) * mm});
            skLineSegment(sketch, "E342", {"start": v(-55.65, 21.43) * mm, "end": v(-52.27, 19.4) * mm});
            skLineSegment(sketch, "E343", {"start": v(-59.9, 34.14) * mm, "end": v(-59.44, 34.43) * mm});
            skLineSegment(sketch, "E344", {"start": v(-59.44, 34.43) * mm, "end": v(-59.44, 34.68) * mm});
            skLineSegment(sketch, "E345", {"start": v(-59.44, 34.68) * mm, "end": v(-59.54, 34.8) * mm});
            skLineSegment(sketch, "E346", {"start": v(-59.54, 34.8) * mm, "end": v(-59.54, 35.02) * mm});
            skLineSegment(sketch, "E347", {"start": v(-59.54, 35.02) * mm, "end": v(-49.35, 39.33) * mm});
            skLineSegment(sketch, "E348", {"start": v(-49.35, 39.33) * mm, "end": v(-39.09, 41.76) * mm});
            skLineSegment(sketch, "E349", {"start": v(-39.09, 41.76) * mm, "end": v(-38.1, 41.76) * mm});
            skLineSegment(sketch, "E350", {"start": v(-38.1, 41.76) * mm, "end": v(-35.9, 39.26) * mm});
            skLineSegment(sketch, "E351", {"start": v(-35.9, 39.26) * mm, "end": v(-33.67, 39.49) * mm});
            skLineSegment(sketch, "E352", {"start": v(-33.67, 39.49) * mm, "end": v(-35.37, 39.49) * mm});
            skLineSegment(sketch, "E353", {"start": v(-35.37, 39.49) * mm, "end": v(-37.33, 41.78) * mm});
            skLineSegment(sketch, "E354", {"start": v(-37.33, 41.78) * mm, "end": v(-37.84, 42) * mm});
            skLineSegment(sketch, "E355", {"start": v(-37.84, 42) * mm, "end": v(-38.86, 42) * mm});
            skLineSegment(sketch, "E356", {"start": v(-39.09, 41.76) * mm, "end": v(-38.86, 42) * mm});
            skLineSegment(sketch, "E357", {"start": v(-33.67, 39.49) * mm, "end": v(-24.42, 40.6) * mm});
            skLineSegment(sketch, "E358", {"start": v(-24.42, 40.6) * mm, "end": v(-24.45, 40.82) * mm});
            skLineSegment(sketch, "E359", {"start": v(-24.45, 40.82) * mm, "end": v(-23.78, 40.9) * mm});
            skLineSegment(sketch, "E360", {"start": v(-23.78, 40.9) * mm, "end": v(-22.17, 40.24) * mm});
            skLineSegment(sketch, "E361", {"start": v(-22.17, 40.24) * mm, "end": v(-20.75, 40.24) * mm});
            skLineSegment(sketch, "E362", {"start": v(-20.75, 40.24) * mm, "end": v(-22.29, 40.86) * mm});
            skLineSegment(sketch, "E363", {"start": v(-22.29, 40.86) * mm, "end": v(-23.68, 40.86) * mm});
            skLineSegment(sketch, "E364", {"start": v(-24.42, 40.6) * mm, "end": v(-22.45, 39.94) * mm});
            skLineSegment(sketch, "E365", {"start": v(-22.45, 39.94) * mm, "end": v(-22.45, 39.6) * mm});
            skLineSegment(sketch, "E366", {"start": v(-22.45, 39.6) * mm, "end": v(-24.42, 39.26) * mm});
            skLineSegment(sketch, "E367", {"start": v(-24.42, 39.26) * mm, "end": v(-26.8, 38.76) * mm});
            skLineSegment(sketch, "E368", {"start": v(-26.8, 38.76) * mm, "end": v(-29.2, 38.22) * mm});
            skLineSegment(sketch, "E369", {"start": v(-29.2, 38.22) * mm, "end": v(-31.1, 37.68) * mm});
            skLineSegment(sketch, "E370", {"start": v(-31.1, 37.68) * mm, "end": v(-33.95, 36.81) * mm});
            skLineSegment(sketch, "E371", {"start": v(-33.95, 36.81) * mm, "end": v(-36.12, 35.8) * mm});
            skLineSegment(sketch, "E372", {"start": v(-36.12, 35.8) * mm, "end": v(-32.15, 34.67) * mm});
            skLineSegment(sketch, "E373", {"start": v(-32.15, 34.67) * mm, "end": v(-28.75, 35.43) * mm});
            skLineSegment(sketch, "E374", {"start": v(-28.75, 35.43) * mm, "end": v(-33.6, 36.61) * mm});
            skLineSegment(sketch, "E375", {"start": v(-33.6, 36.61) * mm, "end": v(-32.04, 37.4) * mm});
            skLineSegment(sketch, "E376", {"start": v(-31.67, 36.15) * mm, "end": v(-27.94, 37.64) * mm});
            skLineSegment(sketch, "E377", {"start": v(-27.94, 37.64) * mm, "end": v(-24.2, 36.72) * mm});
            skLineSegment(sketch, "E378", {"start": v(-28.75, 35.43) * mm, "end": v(-24.2, 36.72) * mm});
            skLineSegment(sketch, "E379", {"start": v(-25.67, 37.08) * mm, "end": v(-26.07, 37.42) * mm});
            skPoint(sketch, "E379.endSnap0", {"position": v(-26.07, 37.18) * mm});
            skLineSegment(sketch, "E380", {"start": v(-26.07, 37.42) * mm, "end": v(-21.82, 38.8) * mm});
            skLineSegment(sketch, "E381", {"start": v(-53.91, 27.53) * mm, "end": v(-42.73, 25.51) * mm});
            skLineSegment(sketch, "E382", {"start": v(-42.73, 25.51) * mm, "end": v(-42.5, 26.75) * mm});
            skLineSegment(sketch, "E383", {"start": v(-42.5, 26.75) * mm, "end": v(-39.29, 27.15) * mm});
            skLineSegment(sketch, "E384", {"start": v(-39.29, 27.15) * mm, "end": v(-39.29, 25.65) * mm});
            skLineSegment(sketch, "E385", {"start": v(-39.29, 25.65) * mm, "end": v(-42.73, 25.51) * mm});
            skLineSegment(sketch, "E386", {"start": v(-39.29, 27.15) * mm, "end": v(-28.12, 25.51) * mm});
            skLineSegment(sketch, "E387", {"start": v(-28.12, 25.51) * mm, "end": v(-10.87, 26.92) * mm});
            skLineSegment(sketch, "E388", {"start": v(-10.87, 26.92) * mm, "end": v(0.17, 32.05) * mm});
            skLineSegment(sketch, "E389", {"start": v(-20.96, 26.1) * mm, "end": v(-15.8, 27.8) * mm});
            skLineSegment(sketch, "E390", {"start": v(-25.93, 26.66) * mm, "end": v(-13.65, 30.43) * mm});
            skPoint(sketch, "E390.endSnap0", {"position": v(-1.26, 30.43) * mm});
            skLineSegment(sketch, "E391", {"start": v(-13.65, 30.43) * mm, "end": v(-17.22, 30.8) * mm});
            skLineSegment(sketch, "E392", {"start": v(-17.22, 30.8) * mm, "end": v(-22.72, 28.98) * mm});
            skLineSegment(sketch, "E393", {"start": v(-22.72, 28.98) * mm, "end": v(-25.86, 29.43) * mm});
            skLineSegment(sketch, "E394", {"start": v(-25.86, 29.43) * mm, "end": v(-33.06, 27.8) * mm});
            skLineSegment(sketch, "E395", {"start": v(-33.06, 27.8) * mm, "end": v(-25.93, 26.66) * mm});
            skLineSegment(sketch, "E396", {"start": v(-36.66, 30.19) * mm, "end": v(-22.98, 34.1) * mm});
            skLineSegment(sketch, "E397", {"start": v(-22.98, 34.1) * mm, "end": v(-15.35, 35.51) * mm});
            skLineSegment(sketch, "E398", {"start": v(-15.35, 35.51) * mm, "end": v(-3.05, 35.99) * mm});
            skLineSegment(sketch, "E399", {"start": v(-21.82, 38.8) * mm, "end": v(-20.17, 39.12) * mm});
            skLineSegment(sketch, "E400", {"start": v(-20.17, 39.12) * mm, "end": v(-20.17, 40.06) * mm});
            skLineSegment(sketch, "E401", {"start": v(-20.17, 40.06) * mm, "end": v(-20.75, 40.24) * mm});
            skLineSegment(sketch, "E402", {"start": v(-20.17, 39.12) * mm, "end": v(-15.34, 39.76) * mm});
            skLineSegment(sketch, "E403", {"start": v(-15.34, 39.76) * mm, "end": v(-15.62, 39.38) * mm});
            skLineSegment(sketch, "E404", {"start": v(-15.34, 39.76) * mm, "end": v(-13.27, 41.14) * mm});
            skLineSegment(sketch, "E405", {"start": v(-13.27, 41.14) * mm, "end": v(-4.67, 46.2) * mm});
            skLineSegment(sketch, "E406", {"start": v(-4.67, 46.2) * mm, "end": v(-1.3, 45.93) * mm});
            skLineSegment(sketch, "E407", {"start": v(-1.3, 45.93) * mm, "end": v(3.25, 45.23) * mm});
            skLineSegment(sketch, "E408", {"start": v(3.25, 45.23) * mm, "end": v(10.22, 43.93) * mm});
            skLineSegment(sketch, "E409", {"start": v(10.22, 43.93) * mm, "end": v(4.01, 37.75) * mm});
            skLineSegment(sketch, "E410", {"start": v(4.01, 37.75) * mm, "end": v(1.8, 37.97) * mm});
            skLineSegment(sketch, "E411", {"start": v(1.8, 37.97) * mm, "end": v(-0.75, 38.31) * mm});
            skLineSegment(sketch, "E412", {"start": v(-0.75, 38.31) * mm, "end": v(-3.64, 38.74) * mm});
            skLineSegment(sketch, "E413", {"start": v(-3.64, 38.74) * mm, "end": v(-5.85, 39.13) * mm});
            skLineSegment(sketch, "E414", {"start": v(-5.85, 39.13) * mm, "end": v(-7.47, 39.42) * mm});
            skLineSegment(sketch, "E415", {"start": v(-7.47, 39.42) * mm, "end": v(-9.28, 39.76) * mm});
            skLineSegment(sketch, "E416", {"start": v(-9.28, 39.76) * mm, "end": v(-11.18, 40.24) * mm});
            skLineSegment(sketch, "E417", {"start": v(-11.18, 40.24) * mm, "end": v(-12.4, 40.67) * mm});
            skLineSegment(sketch, "E418", {"start": v(-12.4, 40.67) * mm, "end": v(-12.72, 40.9) * mm});
            skLineSegment(sketch, "E419", {"start": v(-12.72, 40.9) * mm, "end": v(-4.47, 45.75) * mm});
            skLineSegment(sketch, "E420", {"start": v(-4.47, 45.75) * mm, "end": v(-2.95, 45.63) * mm});
            skLineSegment(sketch, "E421", {"start": v(-2.95, 45.63) * mm, "end": v(3.2, 44.68) * mm});
            skLineSegment(sketch, "E422", {"start": v(3.2, 44.68) * mm, "end": v(9.34, 43.73) * mm});
            skLineSegment(sketch, "E423", {"start": v(9.34, 43.73) * mm, "end": v(3.68, 37.78) * mm});
            skLineSegment(sketch, "E424", {"start": v(7.35, 37.72) * mm, "end": v(12.18, 42.81) * mm});
            skLineSegment(sketch, "E425", {"start": v(12.18, 42.81) * mm, "end": v(24.97, 43.65) * mm});
            skLineSegment(sketch, "E426", {"start": v(24.97, 43.65) * mm, "end": v(32, 43.1) * mm});
            skLineSegment(sketch, "E427", {"start": v(32, 43.1) * mm, "end": v(34.85, 42.88) * mm});
            skLineSegment(sketch, "E428", {"start": v(34.85, 42.88) * mm, "end": v(37.47, 42.24) * mm});
            skLineSegment(sketch, "E429", {"start": v(37.47, 42.24) * mm, "end": v(39.55, 41.14) * mm});
            skLineSegment(sketch, "E430", {"start": v(39.75, 41.14) * mm, "end": v(38.5, 40.19) * mm});
            skLineSegment(sketch, "E431", {"start": v(38.5, 40.19) * mm, "end": v(37.35, 39.5) * mm});
            skLineSegment(sketch, "E432", {"start": v(37.35, 39.5) * mm, "end": v(36.23, 38.89) * mm});
            skLineSegment(sketch, "E433", {"start": v(36.23, 38.89) * mm, "end": v(34.23, 38.1) * mm});
            skLineSegment(sketch, "E434", {"start": v(34.23, 38.1) * mm, "end": v(32.85, 37.7) * mm});
            skLineSegment(sketch, "E435", {"start": v(32.85, 37.7) * mm, "end": v(31.4, 37.47) * mm});
            skLineSegment(sketch, "E436", {"start": v(31.4, 37.47) * mm, "end": v(24.6, 37.47) * mm});
            skLineSegment(sketch, "E437", {"start": v(24.6, 37.47) * mm, "end": v(21.2, 37.47) * mm});
            skLineSegment(sketch, "E438", {"start": v(21.2, 37.47) * mm, "end": v(18.02, 37.47) * mm});
            skLineSegment(sketch, "E439", {"start": v(18.02, 37.47) * mm, "end": v(14.78, 37.47) * mm});
            skLineSegment(sketch, "E440", {"start": v(14.78, 37.47) * mm, "end": v(12.15, 37.47) * mm});
            skLineSegment(sketch, "E441", {"start": v(12.15, 37.47) * mm, "end": v(8.89, 37.42) * mm});
            skLineSegment(sketch, "E442", {"start": v(8.89, 37.42) * mm, "end": v(6.32, 37.42) * mm});
            skLineSegment(sketch, "E443", {"start": v(6.32, 37.42) * mm, "end": v(6.92, 38.48) * mm});
            skLineSegment(sketch, "E444", {"start": v(6.92, 38.48) * mm, "end": v(11.98, 43.57) * mm});
            skLineSegment(sketch, "E445", {"start": v(11.98, 43.57) * mm, "end": v(26.43, 44.03) * mm});
            skLineSegment(sketch, "E446", {"start": v(26.43, 44.03) * mm, "end": v(33.3, 43.48) * mm});
            skLineSegment(sketch, "E447", {"start": v(33.3, 43.48) * mm, "end": v(35.94, 43.07) * mm});
            skLineSegment(sketch, "E448", {"start": v(35.94, 43.07) * mm, "end": v(37.2, 42.76) * mm});
            skLineSegment(sketch, "E449", {"start": v(37.2, 42.76) * mm, "end": v(40.09, 41.28) * mm});
            skLineSegment(sketch, "E450", {"start": v(40.09, 41.28) * mm, "end": v(39.75, 41.14) * mm});
            skLineSegment(sketch, "E451", {"start": v(40.09, 41.28) * mm, "end": v(41.46, 41.84) * mm});
            skLineSegment(sketch, "E452", {"start": v(41.46, 41.84) * mm, "end": v(42.2, 41.84) * mm});
            skLineSegment(sketch, "E453", {"start": v(42.2, 41.84) * mm, "end": v(40.94, 42.58) * mm});
            skLineSegment(sketch, "E454", {"start": v(40.94, 42.58) * mm, "end": v(39.25, 43.32) * mm});
            skLineSegment(sketch, "E455", {"start": v(39.25, 43.32) * mm, "end": v(38.15, 43.59) * mm});
            skLineSegment(sketch, "E456", {"start": v(38.15, 43.59) * mm, "end": v(34.35, 44.1) * mm});
            skLineSegment(sketch, "E457", {"start": v(34.35, 44.1) * mm, "end": v(28.44, 44.55) * mm});
            skLineSegment(sketch, "E458", {"start": v(28.44, 44.55) * mm, "end": v(19.24, 44.69) * mm});
            skLineSegment(sketch, "E459", {"start": v(19.24, 44.69) * mm, "end": v(12.63, 44.39) * mm});
            skLineSegment(sketch, "E460", {"start": v(12.63, 44.39) * mm, "end": v(11.98, 43.57) * mm});
            skLineSegment(sketch, "E461", {"start": v(39.55, 41.14) * mm, "end": v(39.75, 41.14) * mm});
            skLineSegment(sketch, "E462", {"start": v(39.26, 41.3) * mm, "end": v(37.2, 39.97) * mm});
            skLineSegment(sketch, "E463", {"start": v(37.2, 39.97) * mm, "end": v(36.34, 39.46) * mm});
            skLineSegment(sketch, "E464", {"start": v(36.34, 39.46) * mm, "end": v(35.02, 38.89) * mm});
            skLineSegment(sketch, "E465", {"start": v(35.02, 38.89) * mm, "end": v(33.9, 38.37) * mm});
            skLineSegment(sketch, "E466", {"start": v(33.9, 38.37) * mm, "end": v(33.1, 38.18) * mm});
            skLineSegment(sketch, "E467", {"start": v(33.1, 38.18) * mm, "end": v(32.01, 37.94) * mm});
            skLineSegment(sketch, "E468", {"start": v(32.01, 37.94) * mm, "end": v(30.75, 37.72) * mm});
            skLineSegment(sketch, "E469", {"start": v(30.75, 37.72) * mm, "end": v(26.99, 37.67) * mm});
            skLineSegment(sketch, "E470", {"start": v(26.99, 37.67) * mm, "end": v(17.7, 37.67) * mm});
            skLineSegment(sketch, "E471", {"start": v(17.7, 37.67) * mm, "end": v(7.35, 37.72) * mm});
            skLineSegment(sketch, "E472", {"start": v(-4.67, 46.2) * mm, "end": v(0, 47.67) * mm});
            skLineSegment(sketch, "E473", {"start": v(0, 47.67) * mm, "end": v(3.06, 48.45) * mm});
            skLineSegment(sketch, "E474", {"start": v(3.06, 48.45) * mm, "end": v(7.07, 48.94) * mm});
            skLineSegment(sketch, "E475", {"start": v(7.07, 48.94) * mm, "end": v(14.82, 48.94) * mm});
            skLineSegment(sketch, "E476", {"start": v(14.82, 48.94) * mm, "end": v(22.02, 48.04) * mm});
            skLineSegment(sketch, "E477", {"start": v(22.02, 48.04) * mm, "end": v(16.48, 47.94) * mm});
            skLineSegment(sketch, "E478", {"start": v(16.48, 47.94) * mm, "end": v(7.53, 48.19) * mm});
            skLineSegment(sketch, "E479", {"start": v(7.53, 48.19) * mm, "end": v(4.57, 47.48) * mm});
            skLineSegment(sketch, "E480", {"start": v(4.57, 47.48) * mm, "end": v(11.52, 46.7) * mm});
            skLineSegment(sketch, "E481", {"start": v(11.52, 46.7) * mm, "end": v(16.48, 47.94) * mm});
            skLineSegment(sketch, "E482", {"start": v(22.02, 48.04) * mm, "end": v(26.84, 47.67) * mm});
            skLineSegment(sketch, "E483", {"start": v(26.84, 47.67) * mm, "end": v(33.03, 46.5) * mm});
            skLineSegment(sketch, "E484", {"start": v(33.03, 46.5) * mm, "end": v(35.37, 45.93) * mm});
            skLineSegment(sketch, "E485", {"start": v(35.37, 45.93) * mm, "end": v(44.57, 42.88) * mm});
            skLineSegment(sketch, "E486", {"start": v(44.57, 42.88) * mm, "end": v(47.44, 41.62) * mm});
            skLineSegment(sketch, "E487", {"start": v(47.44, 41.62) * mm, "end": v(44.2, 41.87) * mm});
            skLineSegment(sketch, "E488", {"start": v(44.2, 41.87) * mm, "end": v(49.48, 40.8) * mm});
            skLineSegment(sketch, "E489", {"start": v(49.48, 40.8) * mm, "end": v(56.85, 38.89) * mm});
            skLineSegment(sketch, "E490", {"start": v(56.85, 38.89) * mm, "end": v(47.44, 41.62) * mm});
            skLineSegment(sketch, "E491", {"start": v(56.85, 38.89) * mm, "end": v(58.66, 37.96) * mm});
            skLineSegment(sketch, "E492", {"start": v(58.66, 37.96) * mm, "end": v(60.48, 36.55) * mm});
            skLineSegment(sketch, "E493", {"start": v(37.68, 35.7) * mm, "end": v(42.84, 39.67) * mm});
            skLineSegment(sketch, "E494", {"start": v(42.84, 39.67) * mm, "end": v(48.15, 38.83) * mm});
            skLineSegment(sketch, "E495", {"start": v(48.15, 38.83) * mm, "end": v(51.28, 38.34) * mm});
            skLineSegment(sketch, "E496", {"start": v(51.28, 38.34) * mm, "end": v(48.73, 36.8) * mm});
            skLineSegment(sketch, "E497", {"start": v(48.73, 36.8) * mm, "end": v(44.76, 35.5) * mm});
            skLineSegment(sketch, "E498", {"start": v(44.76, 35.5) * mm, "end": v(37.68, 35.7) * mm});
            skLineSegment(sketch, "E499", {"start": v(42.54, 35.57) * mm, "end": v(45.7, 38.89) * mm});
            skLineSegment(sketch, "E500", {"start": v(45.7, 38.89) * mm, "end": v(45.97, 39.17) * mm});
            skLineSegment(sketch, "E501", {"start": v(44.76, 35.5) * mm, "end": v(48.15, 38.83) * mm});
            skLineSegment(sketch, "E502", {"start": v(48.84, 36.77) * mm, "end": v(50, 38.04) * mm});
            skPoint(sketch, "E502.endSnap0", {"position": v(50, 37.58) * mm});
            skLineSegment(sketch, "E503", {"start": v(34.34, 31.05) * mm, "end": v(28.27, 32.25) * mm});
            skLineSegment(sketch, "E504", {"start": v(28.27, 32.25) * mm, "end": v(21.88, 32.98) * mm});
            skLineSegment(sketch, "E505", {"start": v(21.88, 32.98) * mm, "end": v(14.92, 33.78) * mm});
            skLineSegment(sketch, "E506", {"start": v(14.92, 33.78) * mm, "end": v(8.84, 34.22) * mm});
            skLineSegment(sketch, "E507", {"start": v(7.95, 34.96) * mm, "end": v(-9.93, 38.16) * mm});
            skLineSegment(sketch, "E508", {"start": v(-9.93, 38.16) * mm, "end": v(-15.62, 39.38) * mm});
            skLineSegment(sketch, "E509", {"start": v(-9.93, 38.16) * mm, "end": v(3.68, 37.78) * mm});
            skLineSegment(sketch, "E510", {"start": v(-1.02, 33.82) * mm, "end": v(-5.78, 34.67) * mm});
            skLineSegment(sketch, "E511", {"start": v(-5.78, 34.67) * mm, "end": v(-8.52, 34.96) * mm});
            skLineSegment(sketch, "E512", {"start": v(-8.52, 34.96) * mm, "end": v(-37.4, 27.7) * mm});
            skLineSegment(sketch, "E513", {"start": v(-36.66, 30.19) * mm, "end": v(-30.12, 31.55) * mm});
            skLineSegment(sketch, "E514", {"start": v(-30.12, 31.55) * mm, "end": v(-21.7, 33.59) * mm});
            skLineSegment(sketch, "E515", {"start": v(-21.7, 33.59) * mm, "end": v(-15.05, 34.56) * mm});
            skLineSegment(sketch, "E516", {"start": v(-15.05, 34.56) * mm, "end": v(-11.11, 35) * mm});
            skLineSegment(sketch, "E517", {"start": v(-11.11, 35) * mm, "end": v(-8.52, 34.96) * mm});
            skLineSegment(sketch, "E518", {"start": v(-5.78, 34.67) * mm, "end": v(-2.46, 34.96) * mm});
            skLineSegment(sketch, "E519", {"start": v(-2.46, 34.96) * mm, "end": v(-3.05, 35.99) * mm});
            skLineSegment(sketch, "E520", {"start": v(-2.46, 34.96) * mm, "end": v(0, 34.32) * mm});
            skLineSegment(sketch, "E521", {"start": v(0, 34.32) * mm, "end": v(-2.71, 34.12) * mm});
            skLineSegment(sketch, "E522", {"start": v(0, 34.32) * mm, "end": v(-3.02, 36.3) * mm});
            skLineSegment(sketch, "E523", {"start": v(-3.02, 36.3) * mm, "end": v(-13.66, 38.16) * mm});
            skLineSegment(sketch, "E524", {"start": v(-13.66, 38.16) * mm, "end": v(-20.17, 37.41) * mm});
            skLineSegment(sketch, "E525", {"start": v(-20.17, 37.41) * mm, "end": v(-24.2, 36.72) * mm});
            skLineSegment(sketch, "E526", {"start": v(5.28, 35.43) * mm, "end": v(11.77, 35.43) * mm});
            skLineSegment(sketch, "E527", {"start": v(11.77, 35.43) * mm, "end": v(18.81, 34.67) * mm});
            skLineSegment(sketch, "E528", {"start": v(18.81, 34.67) * mm, "end": v(26.44, 34.27) * mm});
            skLineSegment(sketch, "E529", {"start": v(26.44, 34.27) * mm, "end": v(41.41, 32.33) * mm});
            skLineSegment(sketch, "E530", {"start": v(41.41, 32.33) * mm, "end": v(44.28, 32.33) * mm});
            skLineSegment(sketch, "E531", {"start": v(44.28, 32.33) * mm, "end": v(46.71, 32.9) * mm});
            skPoint(sketch, "E531.endSnap0", {"position": v(48.7, 32.9) * mm});
            skLineSegment(sketch, "E532", {"start": v(46.71, 32.9) * mm, "end": v(53.85, 35.63) * mm});
            skLineSegment(sketch, "E533", {"start": v(36.55, 35.7) * mm, "end": v(23.67, 36.12) * mm});
            skLineSegment(sketch, "E534", {"start": v(12.06, 36.46) * mm, "end": v(3.84, 36.46) * mm});
            skLineSegment(sketch, "E535", {"start": v(3.84, 36.46) * mm, "end": v(-3.12, 37.97) * mm});
            skLineSegment(sketch, "E536", {"start": v(50.6, 23.87) * mm, "end": v(52.4, 26.01) * mm});
            skLineSegment(sketch, "E537", {"start": v(52.4, 26.01) * mm, "end": v(54.05, 28.05) * mm});
            skLineSegment(sketch, "E538", {"start": v(54.05, 28.05) * mm, "end": v(56.24, 30.58) * mm});
            skLineSegment(sketch, "E539", {"start": v(56.24, 30.58) * mm, "end": v(58.37, 32.33) * mm});
            skLineSegment(sketch, "E540", {"start": v(58.37, 32.33) * mm, "end": v(60.17, 32.82) * mm});
            skLineSegment(sketch, "E541", {"start": v(60.17, 32.82) * mm, "end": v(60.95, 32.25) * mm});
            skLineSegment(sketch, "E542", {"start": v(44.7, 16.76) * mm, "end": v(41.74, 16.45) * mm});
            skLineSegment(sketch, "E543", {"start": v(41.74, 16.45) * mm, "end": v(40.18, 16.2) * mm});
            skLineSegment(sketch, "E544", {"start": v(40.18, 16.2) * mm, "end": v(38.62, 15.59) * mm});
            skLineSegment(sketch, "E545", {"start": v(38.62, 15.59) * mm, "end": v(36.74, 14.92) * mm});
            skLineSegment(sketch, "E546", {"start": v(36.74, 14.92) * mm, "end": v(35.36, 14.43) * mm});
            skLineSegment(sketch, "E547", {"start": v(35.36, 14.43) * mm, "end": v(32.78, 13.38) * mm});
            skLineSegment(sketch, "E548", {"start": v(-31.7, 37.95) * mm, "end": v(-42.16, 34.34) * mm});
            skPoint(sketch, "E548.startSnap0", {"position": v(-30.15, 37.95) * mm});
            skLineSegment(sketch, "E549", {"start": v(-42.16, 34.34) * mm, "end": v(-44.96, 32.94) * mm});
            skLineSegment(sketch, "E550", {"start": v(-44.96, 32.94) * mm, "end": v(-47.46, 31.69) * mm});
            skLineSegment(sketch, "E551", {"start": v(-47.46, 31.69) * mm, "end": v(-43.92, 33.08) * mm});
            skLineSegment(sketch, "E552", {"start": v(-43.92, 33.08) * mm, "end": v(-37.42, 35.61) * mm});
            skLineSegment(sketch, "E553", {"start": v(-32.15, 34.67) * mm, "end": v(-50.95, 28.66) * mm});
            skLineSegment(sketch, "E554", {"start": v(-47.46, 31.69) * mm, "end": v(-53.73, 29.41) * mm});
            skLineSegment(sketch, "E555", {"start": v(-56.5, 31.69) * mm, "end": v(-46.73, 35.36) * mm});
            skLineSegment(sketch, "E556", {"start": v(-46.73, 35.36) * mm, "end": v(-35.9, 39.26) * mm});
            skLineSegment(sketch, "E557", {"start": v(-35.9, 39.26) * mm, "end": v(-41.53, 38.08) * mm});
            skLineSegment(sketch, "E558", {"start": v(-41.53, 38.08) * mm, "end": v(-46.62, 36.92) * mm});
            skLineSegment(sketch, "E559", {"start": v(-46.62, 36.92) * mm, "end": v(-49.5, 35.89) * mm});
            skLineSegment(sketch, "E560", {"start": v(-49.5, 35.89) * mm, "end": v(-54.9, 34.33) * mm});
            skLineSegment(sketch, "E561", {"start": v(-54.9, 34.33) * mm, "end": v(-57.8, 32.98) * mm});
            skLineSegment(sketch, "E562", {"start": v(-54.9, 34.33) * mm, "end": v(-49.5, 37.63) * mm});
            skLineSegment(sketch, "E563", {"start": v(-49.5, 37.63) * mm, "end": v(-45.82, 39.35) * mm});
            skLineSegment(sketch, "E564", {"start": v(-45.82, 39.35) * mm, "end": v(-41.4, 41.22) * mm});
            skLineSegment(sketch, "E565", {"start": v(-48.7, 39.48) * mm, "end": v(-48.7, 38.96) * mm});
            skLineSegment(sketch, "E566", {"start": v(-48.7, 38.96) * mm, "end": v(-52.4, 37.27) * mm});
            skLineSegment(sketch, "E567", {"start": v(-52.4, 37.27) * mm, "end": v(-52.03, 36.84) * mm});
            skLineSegment(sketch, "E568", {"start": v(-52.03, 36.84) * mm, "end": v(-55.97, 34.71) * mm});
            skLineSegment(sketch, "E569", {"start": v(-55.97, 34.71) * mm, "end": v(-57.06, 36.07) * mm});
            skLineSegment(sketch, "E570", {"start": v(-38.07, 18.92) * mm, "end": v(-34, 13.35) * mm});
            skLineSegment(sketch, "E571", {"start": v(-34, 13.35) * mm, "end": v(-28.68, 12.97) * mm});
            skLineSegment(sketch, "E572", {"start": v(-38.07, 18.92) * mm, "end": v(-29.84, 17.97) * mm});
            skLineSegment(sketch, "E573", {"start": v(-38.07, 18.92) * mm, "end": v(-39.03, 18.92) * mm});
            skLineSegment(sketch, "E574", {"start": v(-39.03, 18.92) * mm, "end": v(-34.29, 13.05) * mm});
            skLineSegment(sketch, "E575", {"start": v(-34.29, 13.05) * mm, "end": v(-31.1, 13.14) * mm});
            skLineSegment(sketch, "E576", {"start": v(-34, 13.35) * mm, "end": v(-34.29, 13.05) * mm});
            skLineSegment(sketch, "E577", {"start": v(-40.63, 25.6) * mm, "end": v(-38.18, 21.1) * mm});
            skLineSegment(sketch, "E578", {"start": v(-38.18, 21.1) * mm, "end": v(-30.35, 20.53) * mm});
            skLineSegment(sketch, "E579", {"start": v(-30.35, 20.53) * mm, "end": v(-30.41, 22.02) * mm});
            skLineSegment(sketch, "E580", {"start": v(-30.41, 22.02) * mm, "end": v(-30.13, 22.65) * mm});
            skLineSegment(sketch, "E581", {"start": v(-30.13, 22.65) * mm, "end": v(-27.92, 23.47) * mm});
            skLineSegment(sketch, "E582", {"start": v(-27.92, 23.47) * mm, "end": v(-31.71, 24.28) * mm});
            skLineSegment(sketch, "E583", {"start": v(-31.71, 24.28) * mm, "end": v(-36.06, 25.05) * mm});
            skLineSegment(sketch, "E584", {"start": v(-36.06, 25.05) * mm, "end": v(-39.29, 25.65) * mm});
            skLineSegment(sketch, "E585", {"start": v(-30.35, 20.53) * mm, "end": v(-27.84, 10.03) * mm});
            skLineSegment(sketch, "E586", {"start": v(-27.84, 10.03) * mm, "end": v(-28.15, 7.15) * mm});
            skLineSegment(sketch, "E587", {"start": v(-26.4, 9.57) * mm, "end": v(-28, 16.26) * mm});
            skLineSegment(sketch, "E588", {"start": v(-28, 16.26) * mm, "end": v(-29.37, 21.96) * mm});
            skLineSegment(sketch, "E589", {"start": v(-29.37, 21.96) * mm, "end": v(-29.04, 22.61) * mm});
            skLineSegment(sketch, "E590", {"start": v(-29.04, 22.61) * mm, "end": v(-19.38, 23.78) * mm});
            skLineSegment(sketch, "E591", {"start": v(-19.42, 23.85) * mm, "end": v(-12.72, 24.16) * mm});
            skLineSegment(sketch, "E592", {"start": v(-12.96, 21.03) * mm, "end": v(-20.93, 18.04) * mm});
            skLineSegment(sketch, "E593", {"start": v(-20.93, 18.04) * mm, "end": v(-24.65, 9.9) * mm});
            skLineSegment(sketch, "E594", {"start": v(-23.13, 10.69) * mm, "end": v(-19.84, 17.89) * mm});
            skLineSegment(sketch, "E595", {"start": v(-19.84, 17.89) * mm, "end": v(-20.93, 18.04) * mm});
            skLineSegment(sketch, "E596", {"start": v(-19.84, 17.89) * mm, "end": v(-13.54, 20.14) * mm});
            skLineSegment(sketch, "E597", {"start": v(-13.54, 20.14) * mm, "end": v(-16.87, 11.38) * mm});
            skLineSegment(sketch, "E598", {"start": v(-23.13, 10.69) * mm, "end": v(-24.65, 9.9) * mm});
            skLineSegment(sketch, "E599", {"start": v(-60.26, 18.33) * mm, "end": v(-63.34, 18.33) * mm});
            skLineSegment(sketch, "E600", {"start": v(-63.34, 18.33) * mm, "end": v(-63.56, 19.9) * mm});
            skLineSegment(sketch, "E601", {"start": v(-63.56, 19.9) * mm, "end": v(-60.9, 20.26) * mm});
            skLineSegment(sketch, "E602", {"start": v(-60.9, 20.26) * mm, "end": v(-59.94, 23.07) * mm});
            skLineSegment(sketch, "E603", {"start": v(-60.9, 20.26) * mm, "end": v(-60.08, 19.97) * mm});
            skLineSegment(sketch, "E604", {"start": v(-14.32, 11.37) * mm, "end": v(-9.72, 21.94) * mm});
            skLineSegment(sketch, "E605", {"start": v(-9.72, 21.94) * mm, "end": v(-6.73, 26.3) * mm});
            skLineSegment(sketch, "E606", {"start": v(-6.49, 20.06) * mm, "end": v(-7.88, 21.14) * mm});
            skLineSegment(sketch, "E607", {"start": v(-4.8, 22.76) * mm, "end": v(-7.26, 23.25) * mm});
            skLineSegment(sketch, "E608", {"start": v(-5.32, 23.33) * mm, "end": v(-6.49, 23.88) * mm});
            skLineSegment(sketch, "E609", {"start": v(-5.32, 23.33) * mm, "end": v(-4.06, 24.47) * mm});
            skLineSegment(sketch, "E610", {"start": v(-4.06, 24.47) * mm, "end": v(-4.88, 25.38) * mm});
            skLineSegment(sketch, "E611", {"start": v(-2.77, 27.23) * mm, "end": v(-1.56, 26.64) * mm});
            skLineSegment(sketch, "E612", {"start": v(-1.54, 26.68) * mm, "end": v(-0.36, 27.32) * mm});
            skLineSegment(sketch, "E613", {"start": v(-0.36, 27.32) * mm, "end": v(-1.07, 28) * mm});
            skLineSegment(sketch, "E614", {"start": v(-8.4, 20.6) * mm, "end": v(-7.17, 20.06) * mm});
            skLineSegment(sketch, "E615", {"start": v(-7.17, 20.06) * mm, "end": v(-7.37, 18.84) * mm});
            skLineSegment(sketch, "E616", {"start": v(-7.37, 18.84) * mm, "end": v(-9.46, 18.98) * mm});
            skLineSegment(sketch, "E617", {"start": v(-7.48, 18.04) * mm, "end": v(-9.62, 18.23) * mm});
            skLineSegment(sketch, "E618", {"start": v(-9.62, 18.23) * mm, "end": v(-10.39, 16.46) * mm});
            skLineSegment(sketch, "E619", {"start": v(-10.39, 16.46) * mm, "end": v(-7.71, 15.15) * mm});
            skLineSegment(sketch, "E620", {"start": v(-10.98, 15.82) * mm, "end": v(-8.64, 14.8) * mm});
            skLineSegment(sketch, "E621", {"start": v(-8.64, 14.8) * mm, "end": v(-8.55, 13.27) * mm});
            skLineSegment(sketch, "E622", {"start": v(-8.55, 13.27) * mm, "end": v(-11.47, 13.53) * mm});
            skLineSegment(sketch, "E623", {"start": v(-11.91, 11.68) * mm, "end": v(-8.36, 9.79) * mm});
            skLineSegment(sketch, "E624", {"start": v(-8.38, 9.77) * mm, "end": v(-7.3, 8.12) * mm});
            skLineSegment(sketch, "E625", {"start": v(-7.3, 8.12) * mm, "end": v(-10.82, 8.41) * mm});
            skLineSegment(sketch, "E626", {"start": v(-10.82, 8.41) * mm, "end": v(-10.13, 7.16) * mm});
            skLineSegment(sketch, "E627", {"start": v(-10.13, 7.16) * mm, "end": v(-8.15, 6.02) * mm});
            skLineSegment(sketch, "E628", {"start": v(-8.15, 6.02) * mm, "end": v(-5.94, 5.63) * mm});
            skLineSegment(sketch, "E629", {"start": v(-5.94, 5.63) * mm, "end": v(-4.79, 5.63) * mm});
            skLineSegment(sketch, "E630", {"start": v(-5.58, 4.23) * mm, "end": v(-2.08, 3.54) * mm});
            skLineSegment(sketch, "E631", {"start": v(-2.08, 3.54) * mm, "end": v(2.48, 3.54) * mm});
            skLineSegment(sketch, "E632", {"start": v(2.48, 3.54) * mm, "end": v(5.11, 5.01) * mm});
            skLineSegment(sketch, "E633", {"start": v(5.11, 5.01) * mm, "end": v(6.67, 6.34) * mm});
            skLineSegment(sketch, "E634", {"start": v(6.67, 6.34) * mm, "end": v(8.12, 8.1) * mm});
            skLineSegment(sketch, "E635", {"start": v(8.12, 8.1) * mm, "end": v(9.25, 10.04) * mm});
            skLineSegment(sketch, "E636", {"start": v(9.25, 10.04) * mm, "end": v(9.68, 11.2) * mm});
            skLineSegment(sketch, "E637", {"start": v(9.68, 11.2) * mm, "end": v(10.08, 12.32) * mm});
            skLineSegment(sketch, "E638", {"start": v(10.08, 12.32) * mm, "end": v(10.57, 14.55) * mm});
            skLineSegment(sketch, "E639", {"start": v(10.57, 14.55) * mm, "end": v(10.8, 18.02) * mm});
            skLineSegment(sketch, "E640", {"start": v(10.8, 18.02) * mm, "end": v(10.4, 20.82) * mm});
            skLineSegment(sketch, "E641", {"start": v(10.4, 20.82) * mm, "end": v(9.85, 22.53) * mm});
            skLineSegment(sketch, "E642", {"start": v(9.85, 22.53) * mm, "end": v(7.66, 25.99) * mm});
            skLineSegment(sketch, "E643", {"start": v(7.1, 26.46) * mm, "end": v(3.84, 27.32) * mm});
            skLineSegment(sketch, "E644", {"start": v(3.84, 27.32) * mm, "end": v(0.08, 26.28) * mm});
            skLineSegment(sketch, "E645", {"start": v(0.08, 26.28) * mm, "end": v(-2.2, 24.84) * mm});
            skLineSegment(sketch, "E646", {"start": v(-2.2, 24.84) * mm, "end": v(-4.45, 22.67) * mm});
            skLineSegment(sketch, "E647", {"start": v(-4.45, 22.67) * mm, "end": v(-5.96, 18.68) * mm});
            skLineSegment(sketch, "E648", {"start": v(-5.96, 18.68) * mm, "end": v(-6.7, 16.14) * mm});
            skLineSegment(sketch, "E649", {"start": v(-6.7, 16.14) * mm, "end": v(-6.97, 14.23) * mm});
            skLineSegment(sketch, "E650", {"start": v(-6.97, 14.23) * mm, "end": v(-6.97, 10.76) * mm});
            skLineSegment(sketch, "E651", {"start": v(-6.97, 10.76) * mm, "end": v(-6.24, 8.25) * mm});
            skLineSegment(sketch, "E652", {"start": v(-6.24, 8.25) * mm, "end": v(-4.79, 5.63) * mm});
            skLineSegment(sketch, "E653", {"start": v(-5.58, 4.23) * mm, "end": v(-8.78, 5.11) * mm});
            skLineSegment(sketch, "E654", {"start": v(-8.78, 5.11) * mm, "end": v(-11, 6.3) * mm});
            skLineSegment(sketch, "E655", {"start": v(-11, 6.3) * mm, "end": v(-12.62, 7.73) * mm});
            skLineSegment(sketch, "E656", {"start": v(-12.62, 7.73) * mm, "end": v(-13.64, 9.34) * mm});
            skLineSegment(sketch, "E657", {"start": v(-13.64, 9.34) * mm, "end": v(-14.32, 11.37) * mm});
            skLineSegment(sketch, "E658", {"start": v(-5.58, 14.42) * mm, "end": v(-5, 17.32) * mm});
            skLineSegment(sketch, "E659", {"start": v(-5, 17.32) * mm, "end": v(-4.14, 19.45) * mm});
            skLineSegment(sketch, "E660", {"start": v(-4.14, 19.45) * mm, "end": v(-2.78, 21.59) * mm});
            skLineSegment(sketch, "E661", {"start": v(-2.78, 21.59) * mm, "end": v(-0.9, 23.68) * mm});
            skLineSegment(sketch, "E662", {"start": v(-0.9, 23.68) * mm, "end": v(1.04, 24.99) * mm});
            skLineSegment(sketch, "E663", {"start": v(1.04, 24.99) * mm, "end": v(2.74, 25.52) * mm});
            skLineSegment(sketch, "E664", {"start": v(2.74, 25.52) * mm, "end": v(5.02, 25.5) * mm});
            skLineSegment(sketch, "E665", {"start": v(5.02, 25.5) * mm, "end": v(8, 23.96) * mm});
            skLineSegment(sketch, "E666", {"start": v(8, 23.96) * mm, "end": v(9.4, 21.96) * mm});
            skLineSegment(sketch, "E667", {"start": v(9.4, 21.96) * mm, "end": v(10.17, 19.9) * mm});
            skLineSegment(sketch, "E668", {"start": v(10.17, 19.9) * mm, "end": v(10.5, 15.87) * mm});
            skLineSegment(sketch, "E669", {"start": v(10.5, 15.87) * mm, "end": v(10.31, 14.95) * mm});
            skLineSegment(sketch, "E670", {"start": v(10.31, 14.95) * mm, "end": v(10.08, 13.76) * mm});
            skLineSegment(sketch, "E671", {"start": v(10.08, 13.76) * mm, "end": v(9.75, 12.14) * mm});
            skLineSegment(sketch, "E672", {"start": v(9.75, 12.14) * mm, "end": v(9.24, 10.78) * mm});
            skLineSegment(sketch, "E673", {"start": v(9.24, 10.78) * mm, "end": v(8.97, 10.26) * mm});
            skLineSegment(sketch, "E674", {"start": v(8.97, 10.26) * mm, "end": v(8.57, 9.6) * mm});
            skLineSegment(sketch, "E675", {"start": v(8.57, 9.6) * mm, "end": v(7.06, 7.32) * mm});
            skLineSegment(sketch, "E676", {"start": v(7.06, 7.32) * mm, "end": v(6.33, 6.6) * mm});
            skLineSegment(sketch, "E677", {"start": v(6.33, 6.6) * mm, "end": v(4.79, 5.39) * mm});
            skLineSegment(sketch, "E678", {"start": v(4.79, 5.39) * mm, "end": v(3.66, 4.84) * mm});
            skLineSegment(sketch, "E679", {"start": v(3.66, 4.84) * mm, "end": v(2.39, 4.33) * mm});
            skLineSegment(sketch, "E680", {"start": v(2.39, 4.33) * mm, "end": v(0.19, 4.15) * mm});
            skLineSegment(sketch, "E681", {"start": v(0.19, 4.15) * mm, "end": v(-1.4, 4.74) * mm});
            skLineSegment(sketch, "E682", {"start": v(-1.4, 4.74) * mm, "end": v(-2.3, 5.36) * mm});
            skLineSegment(sketch, "E683", {"start": v(-2.3, 5.36) * mm, "end": v(-3.6, 6.73) * mm});
            skLineSegment(sketch, "E684", {"start": v(-3.6, 6.73) * mm, "end": v(-4.43, 8.08) * mm});
            skLineSegment(sketch, "E685", {"start": v(-4.43, 8.08) * mm, "end": v(-4.88, 8.81) * mm});
            skLineSegment(sketch, "E686", {"start": v(-4.88, 8.81) * mm, "end": v(-5.24, 10.17) * mm});
            skLineSegment(sketch, "E687", {"start": v(-5.24, 10.17) * mm, "end": v(-5.48, 11.85) * mm});
            skLineSegment(sketch, "E688", {"start": v(-5.48, 11.85) * mm, "end": v(-5.58, 14.42) * mm});
            skLineSegment(sketch, "E689", {"start": v(3.3, 24.46) * mm, "end": v(5.46, 24.2) * mm});
            skLineSegment(sketch, "E690", {"start": v(5.46, 24.2) * mm, "end": v(7.01, 23.42) * mm});
            skLineSegment(sketch, "E691", {"start": v(7.01, 23.42) * mm, "end": v(8.71, 21.4) * mm});
            skLineSegment(sketch, "E692", {"start": v(8.71, 21.4) * mm, "end": v(9.37, 19.31) * mm});
            skLineSegment(sketch, "E693", {"start": v(9.37, 19.31) * mm, "end": v(9.78, 16.27) * mm});
            skLineSegment(sketch, "E694", {"start": v(9.78, 16.27) * mm, "end": v(9.51, 14.43) * mm});
            skLineSegment(sketch, "E695", {"start": v(9.51, 14.43) * mm, "end": v(8.42, 10.85) * mm});
            skLineSegment(sketch, "E696", {"start": v(8.42, 10.85) * mm, "end": v(6.89, 8.67) * mm});
            skLineSegment(sketch, "E697", {"start": v(6.89, 8.67) * mm, "end": v(4.78, 6.58) * mm});
            skLineSegment(sketch, "E698", {"start": v(4.78, 6.58) * mm, "end": v(2.56, 5.53) * mm});
            skLineSegment(sketch, "E699", {"start": v(2.56, 5.53) * mm, "end": v(0.98, 5.53) * mm});
            skLineSegment(sketch, "E700", {"start": v(0.98, 5.53) * mm, "end": v(-0.33, 5.75) * mm});
            skLineSegment(sketch, "E701", {"start": v(-0.33, 5.75) * mm, "end": v(-1.6, 6.43) * mm});
            skLineSegment(sketch, "E702", {"start": v(-1.6, 6.43) * mm, "end": v(-2.8, 7.5) * mm});
            skLineSegment(sketch, "E703", {"start": v(-2.8, 7.5) * mm, "end": v(-3.83, 9.23) * mm});
            skLineSegment(sketch, "E704", {"start": v(-3.83, 9.23) * mm, "end": v(-4.29, 10.59) * mm});
            skLineSegment(sketch, "E705", {"start": v(-4.29, 10.59) * mm, "end": v(-4.46, 11.78) * mm});
            skLineSegment(sketch, "E706", {"start": v(-4.46, 11.78) * mm, "end": v(-4.46, 14.42) * mm});
            skLineSegment(sketch, "E707", {"start": v(-4.46, 14.42) * mm, "end": v(-4.07, 16.76) * mm});
            skLineSegment(sketch, "E708", {"start": v(-4.07, 16.76) * mm, "end": v(-2.95, 19.75) * mm});
            skLineSegment(sketch, "E709", {"start": v(-2.95, 19.75) * mm, "end": v(-1.81, 21.2) * mm});
            skLineSegment(sketch, "E710", {"start": v(-1.81, 21.2) * mm, "end": v(0.28, 23.44) * mm});
            skLineSegment(sketch, "E711", {"start": v(0.28, 23.44) * mm, "end": v(3.3, 24.46) * mm});
            skLineSegment(sketch, "E712", {"start": v(0.76, 6.18) * mm, "end": v(1.21, 7.38) * mm});
            skLineSegment(sketch, "E713", {"start": v(1.21, 7.38) * mm, "end": v(0, 11) * mm});
            skLineSegment(sketch, "E714", {"start": v(0, 11) * mm, "end": v(-0.96, 12.57) * mm});
            skLineSegment(sketch, "E715", {"start": v(-0.96, 12.57) * mm, "end": v(-0.24, 11) * mm});
            skLineSegment(sketch, "E716", {"start": v(-0.24, 11) * mm, "end": v(0.35, 7.82) * mm});
            skLineSegment(sketch, "E717", {"start": v(0.35, 7.82) * mm, "end": v(-0.6, 5.9) * mm});
            skLineSegment(sketch, "E718", {"start": v(1.21, 7.38) * mm, "end": v(-0.93, 8.46) * mm});
            skLineSegment(sketch, "E719", {"start": v(-0.93, 8.46) * mm, "end": v(-2.92, 9.92) * mm});
            skLineSegment(sketch, "E720", {"start": v(-2.92, 9.92) * mm, "end": v(-4.14, 10.25) * mm});
            skLineSegment(sketch, "E721", {"start": v(-4.14, 10.25) * mm, "end": v(-4.2, 10.26) * mm});
            skLineSegment(sketch, "E722", {"start": v(-1.26, 8.72) * mm, "end": v(-1.1, 12.13) * mm});
            skLineSegment(sketch, "E723", {"start": v(-1.1, 12.13) * mm, "end": v(-1.65, 12.9) * mm});
            skLineSegment(sketch, "E724", {"start": v(-1.65, 12.9) * mm, "end": v(-2.14, 13.74) * mm});
            skLineSegment(sketch, "E725", {"start": v(-2.14, 13.74) * mm, "end": v(-1.57, 14.22) * mm});
            skLineSegment(sketch, "E726", {"start": v(-2.14, 13.74) * mm, "end": v(-2.14, 14.27) * mm});
            skLineSegment(sketch, "E727", {"start": v(-2.14, 14.27) * mm, "end": v(-1.64, 14.92) * mm});
            skLineSegment(sketch, "E728", {"start": v(-1.64, 14.92) * mm, "end": v(-1.52, 14.25) * mm});
            skLineSegment(sketch, "E729", {"start": v(-1.52, 14.25) * mm, "end": v(-0.99, 13.6) * mm});
            skLineSegment(sketch, "E730", {"start": v(-0.99, 13.6) * mm, "end": v(-1, 12.55) * mm});
            skLineSegment(sketch, "E731", {"start": v(-1, 12.55) * mm, "end": v(-0.32, 13.14) * mm});
            skLineSegment(sketch, "E732", {"start": v(-0.32, 13.14) * mm, "end": v(0.18, 13.07) * mm});
            skLineSegment(sketch, "E733", {"start": v(0.18, 13.07) * mm, "end": v(0.32, 12.28) * mm});
            skLineSegment(sketch, "E734", {"start": v(0.32, 12.28) * mm, "end": v(0.5, 11.87) * mm});
            skLineSegment(sketch, "E735", {"start": v(0.5, 11.87) * mm, "end": v(1.33, 11.7) * mm});
            skLineSegment(sketch, "E736", {"start": v(1.33, 11.7) * mm, "end": v(2.7, 11.21) * mm});
            skLineSegment(sketch, "E737", {"start": v(2.7, 11.21) * mm, "end": v(2.88, 11.18) * mm});
            skLineSegment(sketch, "E738", {"start": v(2.88, 11.18) * mm, "end": v(5.03, 9.43) * mm});
            skLineSegment(sketch, "E739", {"start": v(5.03, 9.43) * mm, "end": v(3.09, 7.38) * mm});
            skLineSegment(sketch, "E740", {"start": v(3.09, 7.38) * mm, "end": v(3.09, 6.68) * mm});
            skLineSegment(sketch, "E741", {"start": v(3.09, 6.68) * mm, "end": v(0.76, 6.18) * mm});
            skLineSegment(sketch, "E742", {"start": v(-1.42, 15.6) * mm, "end": v(-3, 13.58) * mm});
            skLineSegment(sketch, "E743", {"start": v(-3, 13.58) * mm, "end": v(-4.46, 13.1) * mm});
            skLineSegment(sketch, "E744", {"start": v(-4.35, 15.08) * mm, "end": v(-2.86, 14.7) * mm});
            skLineSegment(sketch, "E745", {"start": v(-2.86, 14.7) * mm, "end": v(-1.28, 16.18) * mm});
            skLineSegment(sketch, "E746", {"start": v(-1.28, 16.18) * mm, "end": v(-1.42, 15.6) * mm});
            skLineSegment(sketch, "E747", {"start": v(-1.64, 14.92) * mm, "end": v(-1.42, 15.6) * mm});
            skLineSegment(sketch, "E748", {"start": v(-0.99, 13.6) * mm, "end": v(-0.32, 13.14) * mm});
            skLineSegment(sketch, "E749", {"start": v(0.18, 13.07) * mm, "end": v(1.23, 13.53) * mm});
            skLineSegment(sketch, "E750", {"start": v(1.23, 13.53) * mm, "end": v(1.94, 14.27) * mm});
            skLineSegment(sketch, "E751", {"start": v(1.94, 14.27) * mm, "end": v(2.26, 14.93) * mm});
            skLineSegment(sketch, "E752", {"start": v(2.44, 16) * mm, "end": v(2.31, 16.95) * mm});
            skLineSegment(sketch, "E753", {"start": v(2.31, 16.95) * mm, "end": v(1.9, 17.55) * mm});
            skLineSegment(sketch, "E754", {"start": v(1.9, 17.55) * mm, "end": v(1.26, 18.07) * mm});
            skLineSegment(sketch, "E755", {"start": v(1.26, 18.07) * mm, "end": v(0.58, 18.1) * mm});
            skLineSegment(sketch, "E756", {"start": v(0.58, 18.1) * mm, "end": v(-0.09, 17.66) * mm});
            skLineSegment(sketch, "E757", {"start": v(-0.09, 17.66) * mm, "end": v(-0.6, 16.96) * mm});
            skLineSegment(sketch, "E758", {"start": v(-0.6, 16.96) * mm, "end": v(-1.01, 16.48) * mm});
            skLineSegment(sketch, "E759", {"start": v(-1.01, 16.48) * mm, "end": v(-1.27, 16.14) * mm});
            skLineSegment(sketch, "E760", {"start": v(-2.86, 14.7) * mm, "end": v(-1.9, 19.65) * mm});
            skLineSegment(sketch, "E761", {"start": v(-1.9, 19.65) * mm, "end": v(-1.81, 21.2) * mm});
            skLineSegment(sketch, "E762", {"start": v(-2.42, 17) * mm, "end": v(-1.25, 17.23) * mm});
            skLineSegment(sketch, "E763", {"start": v(-1.25, 17.23) * mm, "end": v(-0.98, 17.9) * mm});
            skLineSegment(sketch, "E764", {"start": v(-0.98, 17.9) * mm, "end": v(0.58, 18.1) * mm});
            skLineSegment(sketch, "E765", {"start": v(2.25, 27.93) * mm, "end": v(3.62, 27.93) * mm});
            skLineSegment(sketch, "E766", {"start": v(3.62, 27.93) * mm, "end": v(3.02, 28.85) * mm});
            skLineSegment(sketch, "E767", {"start": v(2.25, 27.93) * mm, "end": v(1.65, 28.55) * mm});
            skLineSegment(sketch, "E768", {"start": v(4.82, 27.98) * mm, "end": v(7.1, 26.46) * mm});
            skLineSegment(sketch, "E769", {"start": v(4.82, 27.98) * mm, "end": v(3.03, 30.77) * mm});
            skLineSegment(sketch, "E770", {"start": v(0.58, 18.1) * mm, "end": v(1.75, 19.7) * mm});
            skLineSegment(sketch, "E771", {"start": v(1.75, 19.7) * mm, "end": v(0.91, 21.74) * mm});
            skLineSegment(sketch, "E772", {"start": v(0.91, 21.74) * mm, "end": v(0.91, 23.66) * mm});
            skLineSegment(sketch, "E773", {"start": v(1.58, 17.81) * mm, "end": v(2.95, 19.81) * mm});
            skLineSegment(sketch, "E774", {"start": v(2.95, 19.81) * mm, "end": v(2.95, 22.26) * mm});
            skLineSegment(sketch, "E775", {"start": v(2.95, 22.26) * mm, "end": v(5.96, 23.2) * mm});
            skLineSegment(sketch, "E776", {"start": v(5.96, 23.2) * mm, "end": v(7.4, 21.68) * mm});
            skLineSegment(sketch, "E777", {"start": v(7.4, 21.68) * mm, "end": v(5.31, 18.55) * mm});
            skLineSegment(sketch, "E778", {"start": v(5.31, 18.55) * mm, "end": v(2.82, 17.43) * mm});
            skLineSegment(sketch, "E779", {"start": v(2.82, 17.43) * mm, "end": v(2.08, 17.4) * mm});
            skLineSegment(sketch, "E780", {"start": v(1.75, 19.7) * mm, "end": v(2.95, 19.81) * mm});
            skLineSegment(sketch, "E781", {"start": v(2.94, 22.25) * mm, "end": v(1.75, 22.1) * mm});
            skLineSegment(sketch, "E782", {"start": v(1.75, 22.1) * mm, "end": v(2.35, 19.75) * mm});
            skLineSegment(sketch, "E783", {"start": v(1.75, 22.1) * mm, "end": v(1.96, 24.01) * mm});
            skPoint(sketch, "E783.endSnap0", {"position": v(1.96, 26.8) * mm});
            skLineSegment(sketch, "E784", {"start": v(2.26, 14.93) * mm, "end": v(2.44, 16) * mm});
            skLineSegment(sketch, "E785", {"start": v(2.29, 15.06) * mm, "end": v(3.33, 15.06) * mm});
            skLineSegment(sketch, "E786", {"start": v(3.33, 15.06) * mm, "end": v(5.34, 16) * mm});
            skLineSegment(sketch, "E787", {"start": v(5.34, 16) * mm, "end": v(7.86, 17.34) * mm});
            skLineSegment(sketch, "E788", {"start": v(7.86, 17.34) * mm, "end": v(8.52, 14.57) * mm});
            skLineSegment(sketch, "E789", {"start": v(8.52, 14.57) * mm, "end": v(7.6, 11.58) * mm});
            skLineSegment(sketch, "E790", {"start": v(7.86, 17.34) * mm, "end": v(7.5, 19.42) * mm});
            skLineSegment(sketch, "E791", {"start": v(2.57, 16.2) * mm, "end": v(3.21, 16.3) * mm});
            skLineSegment(sketch, "E792", {"start": v(3.21, 16.3) * mm, "end": v(5.22, 17) * mm});
            skLineSegment(sketch, "E793", {"start": v(5.22, 17) * mm, "end": v(5.34, 16) * mm});
            skLineSegment(sketch, "E794", {"start": v(2.38, 16.47) * mm, "end": v(5.2, 17.46) * mm});
            skLineSegment(sketch, "E795", {"start": v(5.2, 17.46) * mm, "end": v(7, 20.37) * mm});
            skLineSegment(sketch, "E796", {"start": v(7, 20.37) * mm, "end": v(8.29, 21.9) * mm});
            skLineSegment(sketch, "E797", {"start": v(5.03, 9.43) * mm, "end": v(6.64, 11.12) * mm});
            skLineSegment(sketch, "E798", {"start": v(6.64, 11.12) * mm, "end": v(3.75, 6.77) * mm});
            skLineSegment(sketch, "E799", {"start": v(3.75, 6.77) * mm, "end": v(3.19, 6.67) * mm});
            skLineSegment(sketch, "E800", {"start": v(6.64, 11.17) * mm, "end": v(7.09, 11.96) * mm});
            skLineSegment(sketch, "E801", {"start": v(7.09, 11.96) * mm, "end": v(7.6, 11.58) * mm});
            skLineSegment(sketch, "E802", {"start": v(7.09, 11.96) * mm, "end": v(4.18, 12.14) * mm});
            skLineSegment(sketch, "E803", {"start": v(4.18, 12.14) * mm, "end": v(1.68, 12.88) * mm});
            skLineSegment(sketch, "E804", {"start": v(1.68, 12.88) * mm, "end": v(1.43, 13.74) * mm});
            skLineSegment(sketch, "E805", {"start": v(1.14, 13.49) * mm, "end": v(1.2, 12.99) * mm});
            skLineSegment(sketch, "E806", {"start": v(1.2, 12.99) * mm, "end": v(1.35, 12.67) * mm});
            skLineSegment(sketch, "E807", {"start": v(1.35, 12.67) * mm, "end": v(2.9, 12.19) * mm});
            skLineSegment(sketch, "E808", {"start": v(2.9, 12.19) * mm, "end": v(4.58, 11.48) * mm});
            skLineSegment(sketch, "E809", {"start": v(4.58, 11.48) * mm, "end": v(6.64, 11.17) * mm});
            skLineSegment(sketch, "E810", {"start": v(6.64, 11.12) * mm, "end": v(6.64, 11.17) * mm});
            skLineSegment(sketch, "E811", {"start": v(2.88, 11.18) * mm, "end": v(3.74, 11.84) * mm});
            skLineSegment(sketch, "E812", {"start": v(47.32, 14.7) * mm, "end": v(50.97, 14.7) * mm});
            skLineSegment(sketch, "E813", {"start": v(50.97, 14.7) * mm, "end": v(51.33, 16.26) * mm});
            skLineSegment(sketch, "E814", {"start": v(51.33, 16.26) * mm, "end": v(48.17, 17.79) * mm});
            skLineSegment(sketch, "E815", {"start": v(48.17, 17.79) * mm, "end": v(49, 19.43) * mm});
            skLineSegment(sketch, "E816", {"start": v(49, 19.43) * mm, "end": v(51.57, 19.6) * mm});
            skLineSegment(sketch, "E817", {"start": v(51.57, 19.6) * mm, "end": v(52.25, 21) * mm});
            skLineSegment(sketch, "E818", {"start": v(52.25, 21) * mm, "end": v(50.87, 21.67) * mm});
            skLineSegment(sketch, "E819", {"start": v(53.02, 24.36) * mm, "end": v(53.66, 23.88) * mm});
            skLineSegment(sketch, "E820", {"start": v(53.66, 23.88) * mm, "end": v(54.46, 24.94) * mm});
            skLineSegment(sketch, "E821", {"start": v(54.46, 24.94) * mm, "end": v(53.98, 25.76) * mm});
            skLineSegment(sketch, "E822", {"start": v(55.32, 27.28) * mm, "end": v(56.4, 26.47) * mm});
            skLineSegment(sketch, "E823", {"start": v(56.4, 26.48) * mm, "end": v(57.89, 27.33) * mm});
            skLineSegment(sketch, "E824", {"start": v(57.89, 27.33) * mm, "end": v(57.63, 28) * mm});
            skLineSegment(sketch, "E825", {"start": v(57.63, 28) * mm, "end": v(57.47, 28.4) * mm});
            skLineSegment(sketch, "E826", {"start": v(61.89, 26.5) * mm, "end": v(60.83, 27.14) * mm});
            skLineSegment(sketch, "E827", {"start": v(60.83, 27.14) * mm, "end": v(60.25, 27.22) * mm});
            skLineSegment(sketch, "E828", {"start": v(60.25, 27.22) * mm, "end": v(59.39, 27.23) * mm});
            skLineSegment(sketch, "E829", {"start": v(59.39, 27.23) * mm, "end": v(58.7, 27.14) * mm});
            skLineSegment(sketch, "E830", {"start": v(58.7, 27.14) * mm, "end": v(58.19, 26.98) * mm});
            skLineSegment(sketch, "E831", {"start": v(58.19, 26.98) * mm, "end": v(57.5, 26.65) * mm});
            skLineSegment(sketch, "E832", {"start": v(57.5, 26.65) * mm, "end": v(56.8, 25.98) * mm});
            skLineSegment(sketch, "E833", {"start": v(56.8, 25.98) * mm, "end": v(56.06, 25.25) * mm});
            skLineSegment(sketch, "E834", {"start": v(56.06, 25.25) * mm, "end": v(55.17, 23.86) * mm});
            skLineSegment(sketch, "E835", {"start": v(55.17, 23.86) * mm, "end": v(54.75, 23.09) * mm});
            skLineSegment(sketch, "E836", {"start": v(54.75, 23.09) * mm, "end": v(54.35, 22.25) * mm});
            skLineSegment(sketch, "E837", {"start": v(54.35, 22.25) * mm, "end": v(53.65, 20.8) * mm});
            skLineSegment(sketch, "E838", {"start": v(53.65, 20.8) * mm, "end": v(53.04, 18.5) * mm});
            skLineSegment(sketch, "E839", {"start": v(53.04, 18.5) * mm, "end": v(52.53, 16.3) * mm});
            skLineSegment(sketch, "E840", {"start": v(52.53, 16.3) * mm, "end": v(52.53, 14) * mm});
            skLineSegment(sketch, "E841", {"start": v(52.53, 14) * mm, "end": v(52.62, 11.24) * mm});
            skLineSegment(sketch, "E842", {"start": v(52.62, 11.24) * mm, "end": v(54.27, 7.93) * mm});
            skLineSegment(sketch, "E843", {"start": v(54.27, 7.93) * mm, "end": v(55.74, 7.17) * mm});
            skLineSegment(sketch, "E844", {"start": v(55.74, 7.17) * mm, "end": v(57.13, 6.78) * mm});
            skLineSegment(sketch, "E845", {"start": v(57.13, 6.78) * mm, "end": v(58.82, 6.98) * mm});
            skLineSegment(sketch, "E846", {"start": v(58.82, 6.98) * mm, "end": v(59.68, 7.5) * mm});
            skLineSegment(sketch, "E847", {"start": v(59.68, 7.5) * mm, "end": v(60.96, 9.12) * mm});
            skLineSegment(sketch, "E848", {"start": v(60.96, 9.12) * mm, "end": v(61.56, 10.03) * mm});
            skLineSegment(sketch, "E849", {"start": v(61.56, 10.03) * mm, "end": v(62.35, 11.81) * mm});
            skLineSegment(sketch, "E850", {"start": v(62.35, 11.81) * mm, "end": v(62.9, 13.39) * mm});
            skLineSegment(sketch, "E851", {"start": v(62.9, 13.39) * mm, "end": v(63.3, 15.53) * mm});
            skLineSegment(sketch, "E852", {"start": v(63.3, 15.53) * mm, "end": v(63.56, 18.35) * mm});
            skLineSegment(sketch, "E853", {"start": v(63.56, 18.35) * mm, "end": v(63.56, 20.44) * mm});
            skLineSegment(sketch, "E854", {"start": v(63.56, 20.44) * mm, "end": v(63.09, 24.12) * mm});
            skLineSegment(sketch, "E855", {"start": v(63.09, 24.12) * mm, "end": v(62.16, 26.26) * mm});
            skLineSegment(sketch, "E856", {"start": v(53.38, 14.67) * mm, "end": v(53.52, 16.08) * mm});
            skLineSegment(sketch, "E857", {"start": v(53.52, 16.08) * mm, "end": v(53.66, 17.62) * mm});
            skLineSegment(sketch, "E858", {"start": v(53.66, 17.62) * mm, "end": v(54.03, 19.02) * mm});
            skLineSegment(sketch, "E859", {"start": v(54.03, 19.02) * mm, "end": v(54.45, 20.34) * mm});
            skLineSegment(sketch, "E860", {"start": v(54.45, 20.34) * mm, "end": v(55.1, 21.73) * mm});
            skLineSegment(sketch, "E861", {"start": v(55.1, 21.73) * mm, "end": v(55.95, 23.31) * mm});
            skLineSegment(sketch, "E862", {"start": v(55.95, 23.31) * mm, "end": v(57.07, 24.77) * mm});
            skLineSegment(sketch, "E863", {"start": v(57.07, 24.77) * mm, "end": v(58.52, 25.88) * mm});
            skLineSegment(sketch, "E864", {"start": v(58.52, 25.88) * mm, "end": v(59.74, 26.22) * mm});
            skLineSegment(sketch, "E865", {"start": v(59.74, 26.22) * mm, "end": v(60.84, 26.12) * mm});
            skLineSegment(sketch, "E866", {"start": v(60.84, 26.12) * mm, "end": v(61.9, 25.38) * mm});
            skLineSegment(sketch, "E867", {"start": v(61.9, 25.38) * mm, "end": v(62.67, 24.1) * mm});
            skLineSegment(sketch, "E868", {"start": v(62.67, 24.1) * mm, "end": v(63.2, 22.91) * mm});
            skLineSegment(sketch, "E869", {"start": v(63.2, 22.91) * mm, "end": v(63.33, 22.09) * mm});
            skLineSegment(sketch, "E870", {"start": v(63.37, 16.62) * mm, "end": v(63.23, 15.17) * mm});
            skLineSegment(sketch, "E871", {"start": v(63.23, 15.17) * mm, "end": v(62.87, 14.35) * mm});
            skLineSegment(sketch, "E872", {"start": v(62.87, 14.35) * mm, "end": v(62.65, 13.59) * mm});
            skLineSegment(sketch, "E873", {"start": v(62.65, 13.59) * mm, "end": v(62.39, 12.79) * mm});
            skLineSegment(sketch, "E874", {"start": v(62.39, 12.79) * mm, "end": v(61.86, 11.4) * mm});
            skLineSegment(sketch, "E875", {"start": v(61.86, 11.4) * mm, "end": v(61.16, 10.12) * mm});
            skLineSegment(sketch, "E876", {"start": v(61.16, 10.12) * mm, "end": v(60.24, 8.66) * mm});
            skLineSegment(sketch, "E877", {"start": v(60.24, 8.66) * mm, "end": v(59.54, 7.92) * mm});
            skLineSegment(sketch, "E878", {"start": v(59.54, 7.92) * mm, "end": v(58.58, 7.3) * mm});
            skLineSegment(sketch, "E879", {"start": v(58.58, 7.3) * mm, "end": v(57.53, 7.03) * mm});
            skLineSegment(sketch, "E880", {"start": v(57.53, 7.03) * mm, "end": v(56.87, 7) * mm});
            skLineSegment(sketch, "E881", {"start": v(56.87, 7) * mm, "end": v(55.97, 7.15) * mm});
            skLineSegment(sketch, "E882", {"start": v(55.97, 7.15) * mm, "end": v(55, 7.94) * mm});
            skLineSegment(sketch, "E883", {"start": v(55, 7.94) * mm, "end": v(53.54, 11.16) * mm});
            skLineSegment(sketch, "E884", {"start": v(53.54, 11.16) * mm, "end": v(53.34, 13.05) * mm});
            skLineSegment(sketch, "E885", {"start": v(53.34, 13.05) * mm, "end": v(53.38, 14.8) * mm});
            skLineSegment(sketch, "E886", {"start": v(46.5, 10.48) * mm, "end": v(47.15, 9.66) * mm});
            skLineSegment(sketch, "E887", {"start": v(47.15, 9.66) * mm, "end": v(48.35, 8.48) * mm});
            skLineSegment(sketch, "E888", {"start": v(48.35, 8.48) * mm, "end": v(49.94, 7.64) * mm});
            skLineSegment(sketch, "E889", {"start": v(49.94, 7.64) * mm, "end": v(51.84, 7.3) * mm});
            skLineSegment(sketch, "E890", {"start": v(51.84, 7.3) * mm, "end": v(53.7, 7.15) * mm});
            skLineSegment(sketch, "E891", {"start": v(53.7, 7.15) * mm, "end": v(55.19, 6.97) * mm});
            skLineSegment(sketch, "E892", {"start": v(55.19, 6.97) * mm, "end": v(57.2, 6.77) * mm});
            skLineSegment(sketch, "E893", {"start": v(47.32, 14.7) * mm, "end": v(47.32, 13.03) * mm});
            skLineSegment(sketch, "E894", {"start": v(47.32, 13.03) * mm, "end": v(51.26, 11.72) * mm});
            skLineSegment(sketch, "E895", {"start": v(51.26, 11.72) * mm, "end": v(51.4, 10.42) * mm});
            skLineSegment(sketch, "E896", {"start": v(51.4, 10.42) * mm, "end": v(48.3, 10.16) * mm});
            skLineSegment(sketch, "E897", {"start": v(48.3, 10.16) * mm, "end": v(48.33, 9.18) * mm});
            skLineSegment(sketch, "E898", {"start": v(48.33, 9.18) * mm, "end": v(52.18, 8.24) * mm});
            skLineSegment(sketch, "E899", {"start": v(54.41, 11.08) * mm, "end": v(54.41, 12.56) * mm});
            skLineSegment(sketch, "E900", {"start": v(54.41, 12.56) * mm, "end": v(54.13, 15.27) * mm});
            skLineSegment(sketch, "E901", {"start": v(54.13, 15.27) * mm, "end": v(54.7, 18.9) * mm});
            skLineSegment(sketch, "E902", {"start": v(54.7, 18.9) * mm, "end": v(55.56, 21.23) * mm});
            skLineSegment(sketch, "E903", {"start": v(55.56, 21.23) * mm, "end": v(56.7, 23.14) * mm});
            skLineSegment(sketch, "E904", {"start": v(56.7, 23.14) * mm, "end": v(58.13, 24.81) * mm});
            skLineSegment(sketch, "E905", {"start": v(58.13, 24.81) * mm, "end": v(59.56, 25.24) * mm});
            skLineSegment(sketch, "E906", {"start": v(59.56, 25.24) * mm, "end": v(61.14, 24.86) * mm});
            skLineSegment(sketch, "E907", {"start": v(61.14, 24.86) * mm, "end": v(62.18, 23.14) * mm});
            skLineSegment(sketch, "E908", {"start": v(62.18, 23.14) * mm, "end": v(62.85, 21.14) * mm});
            skLineSegment(sketch, "E909", {"start": v(62.85, 21.14) * mm, "end": v(62.85, 18.18) * mm});
            skLineSegment(sketch, "E910", {"start": v(62.85, 18.18) * mm, "end": v(62.47, 15.32) * mm});
            skLineSegment(sketch, "E911", {"start": v(62.47, 15.32) * mm, "end": v(61.42, 12.18) * mm});
            skLineSegment(sketch, "E912", {"start": v(61.42, 12.18) * mm, "end": v(60.37, 10.17) * mm});
            skLineSegment(sketch, "E913", {"start": v(60.37, 10.17) * mm, "end": v(58.6, 8.36) * mm});
            skLineSegment(sketch, "E914", {"start": v(58.6, 8.36) * mm, "end": v(57.18, 7.88) * mm});
            skLineSegment(sketch, "E915", {"start": v(57.18, 7.88) * mm, "end": v(55.51, 8.8) * mm});
            skLineSegment(sketch, "E916", {"start": v(55.51, 8.8) * mm, "end": v(54.39, 11.1) * mm});
            skLineSegment(sketch, "E917", {"start": v(54.41, 12.56) * mm, "end": v(55.83, 10.96) * mm});
            skLineSegment(sketch, "E918", {"start": v(55.83, 10.96) * mm, "end": v(55.76, 13.92) * mm});
            skLineSegment(sketch, "E919", {"start": v(55.76, 13.92) * mm, "end": v(56.07, 15.3) * mm});
            skLineSegment(sketch, "E920", {"start": v(56.07, 15.3) * mm, "end": v(56.55, 15.37) * mm});
            skLineSegment(sketch, "E921", {"start": v(56.55, 15.37) * mm, "end": v(56.93, 15.63) * mm});
            skLineSegment(sketch, "E922", {"start": v(56.93, 15.63) * mm, "end": v(57.17, 16.13) * mm});
            skLineSegment(sketch, "E923", {"start": v(57.17, 16.13) * mm, "end": v(57.36, 16.6) * mm});
            skLineSegment(sketch, "E924", {"start": v(57.36, 16.6) * mm, "end": v(57.38, 17.75) * mm});
            skLineSegment(sketch, "E925", {"start": v(57.38, 17.75) * mm, "end": v(57.15, 18.28) * mm});
            skLineSegment(sketch, "E926", {"start": v(57.15, 18.28) * mm, "end": v(56.74, 18.52) * mm});
            skLineSegment(sketch, "E927", {"start": v(56.74, 18.52) * mm, "end": v(56.38, 18.52) * mm});
            skLineSegment(sketch, "E928", {"start": v(56.38, 18.52) * mm, "end": v(56.07, 17.9) * mm});
            skLineSegment(sketch, "E929", {"start": v(56.07, 17.9) * mm, "end": v(55.86, 17.11) * mm});
            skLineSegment(sketch, "E930", {"start": v(55.86, 17.11) * mm, "end": v(55.79, 16.54) * mm});
            skLineSegment(sketch, "E931", {"start": v(55.79, 16.54) * mm, "end": v(55.86, 15.97) * mm});
            skLineSegment(sketch, "E932", {"start": v(55.86, 15.97) * mm, "end": v(56.2, 15.42) * mm});
            skLineSegment(sketch, "E933", {"start": v(56.2, 15.42) * mm, "end": v(56.55, 15.37) * mm});
            skLineSegment(sketch, "E934", {"start": v(56.18, 13.29) * mm, "end": v(57.22, 10) * mm});
            skLineSegment(sketch, "E935", {"start": v(57.22, 10) * mm, "end": v(57.04, 8.88) * mm});
            skLineSegment(sketch, "E936", {"start": v(57.04, 8.88) * mm, "end": v(58.2, 9.05) * mm});
            skLineSegment(sketch, "E937", {"start": v(58.2, 9.05) * mm, "end": v(58.16, 9.58) * mm});
            skLineSegment(sketch, "E938", {"start": v(58.16, 9.58) * mm, "end": v(60.95, 13.36) * mm});
            skLineSegment(sketch, "E939", {"start": v(60.95, 13.36) * mm, "end": v(59, 9.47) * mm});
            skLineSegment(sketch, "E940", {"start": v(59, 9.47) * mm, "end": v(59.02, 9.03) * mm});
            skLineSegment(sketch, "E941", {"start": v(59.02, 9.03) * mm, "end": v(58.2, 9.05) * mm});
            skLineSegment(sketch, "E942", {"start": v(56.18, 13.29) * mm, "end": v(56.69, 10.06) * mm});
            skLineSegment(sketch, "E943", {"start": v(56.69, 10.06) * mm, "end": v(55.9, 8.58) * mm});
            skLineSegment(sketch, "E944", {"start": v(58.2, 9.05) * mm, "end": v(58, 8.16) * mm});
            skLineSegment(sketch, "E945", {"start": v(60.95, 13.36) * mm, "end": v(61.22, 11.8) * mm});
            skLineSegment(sketch, "E946", {"start": v(60.95, 13.37) * mm, "end": v(61.29, 13.93) * mm});
            skLineSegment(sketch, "E947", {"start": v(61.29, 13.93) * mm, "end": v(61.46, 14.52) * mm});
            skLineSegment(sketch, "E948", {"start": v(61.46, 14.52) * mm, "end": v(61.66, 15.15) * mm});
            skLineSegment(sketch, "E949", {"start": v(61.66, 15.15) * mm, "end": v(61.76, 15.82) * mm});
            skLineSegment(sketch, "E950", {"start": v(61.76, 15.82) * mm, "end": v(61.96, 16.95) * mm});
            skLineSegment(sketch, "E951", {"start": v(61.96, 16.95) * mm, "end": v(61.96, 18.1) * mm});
            skLineSegment(sketch, "E952", {"start": v(61.96, 18.1) * mm, "end": v(61.86, 18.42) * mm});
            skLineSegment(sketch, "E953", {"start": v(61.82, 16.14) * mm, "end": v(62.19, 15.56) * mm});
            skLineSegment(sketch, "E954", {"start": v(62.19, 15.56) * mm, "end": v(62.67, 16.8) * mm});
            skLineSegment(sketch, "E955", {"start": v(61.84, 18.48) * mm, "end": v(61.93, 19.49) * mm});
            skLineSegment(sketch, "E956", {"start": v(61.86, 18.42) * mm, "end": v(61.84, 18.48) * mm});
            skLineSegment(sketch, "E957", {"start": v(57.36, 16.6) * mm, "end": v(57.86, 16.6) * mm});
            skLineSegment(sketch, "E958", {"start": v(57.86, 16.6) * mm, "end": v(59.76, 17.53) * mm});
            skLineSegment(sketch, "E959", {"start": v(59.76, 17.53) * mm, "end": v(59.86, 17.48) * mm});
            skLineSegment(sketch, "E960", {"start": v(59.86, 17.48) * mm, "end": v(60.02, 17.59) * mm});
            skLineSegment(sketch, "E961", {"start": v(60.02, 17.59) * mm, "end": v(61.87, 18.87) * mm});
            skLineSegment(sketch, "E962", {"start": v(57.38, 17.75) * mm, "end": v(59.9, 18.9) * mm});
            skLineSegment(sketch, "E963", {"start": v(59.9, 18.9) * mm, "end": v(59.95, 19.26) * mm});
            skLineSegment(sketch, "E964", {"start": v(59.95, 19.26) * mm, "end": v(61.34, 21.25) * mm});
            skLineSegment(sketch, "E965", {"start": v(61.34, 21.25) * mm, "end": v(61.34, 21.77) * mm});
            skLineSegment(sketch, "E966", {"start": v(61.34, 21.77) * mm, "end": v(61.87, 22.31) * mm});
            skLineSegment(sketch, "E967", {"start": v(61.87, 22.31) * mm, "end": v(60.74, 24.02) * mm});
            skLineSegment(sketch, "E968", {"start": v(60.97, 23.67) * mm, "end": v(58.47, 23.12) * mm});
            skLineSegment(sketch, "E969", {"start": v(58.47, 23.12) * mm, "end": v(58.47, 24.91) * mm});
            skLineSegment(sketch, "E970", {"start": v(58.47, 23.12) * mm, "end": v(58.3, 21.14) * mm});
            skLineSegment(sketch, "E971", {"start": v(58.3, 21.14) * mm, "end": v(57.37, 19.96) * mm});
            skLineSegment(sketch, "E972", {"start": v(57.37, 19.96) * mm, "end": v(56.91, 18.69) * mm});
            skLineSegment(sketch, "E973", {"start": v(56.91, 18.69) * mm, "end": v(56.73, 18.5) * mm});
            skLineSegment(sketch, "E974", {"start": v(57, 18.91) * mm, "end": v(57.34, 18.69) * mm});
            skLineSegment(sketch, "E975", {"start": v(57.34, 18.69) * mm, "end": v(59.7, 19.76) * mm});
            skLineSegment(sketch, "E976", {"start": v(59.7, 19.76) * mm, "end": v(60.78, 21.28) * mm});
            skLineSegment(sketch, "E977", {"start": v(60.78, 21.28) * mm, "end": v(60.85, 21.84) * mm});
            skLineSegment(sketch, "E978", {"start": v(60.85, 21.84) * mm, "end": v(61.54, 22.81) * mm});
            skLineSegment(sketch, "E979", {"start": v(59.16, 23.28) * mm, "end": v(58.64, 21.09) * mm});
            skLineSegment(sketch, "E980", {"start": v(58.64, 21.09) * mm, "end": v(57.37, 19.96) * mm});
            skLineSegment(sketch, "E981", {"start": v(57.6, 24.2) * mm, "end": v(57.8, 20.96) * mm});
            skPoint(sketch, "E981.endSnap0", {"position": v(57.8, 25.33) * mm});
            skLineSegment(sketch, "E982", {"start": v(57.8, 20.96) * mm, "end": v(57.02, 20.4) * mm});
            skLineSegment(sketch, "E983", {"start": v(57.02, 20.4) * mm, "end": v(56.48, 19.66) * mm});
            skLineSegment(sketch, "E984", {"start": v(56.48, 19.66) * mm, "end": v(56.22, 19.46) * mm});
            skLineSegment(sketch, "E985", {"start": v(56.22, 19.46) * mm, "end": v(55.32, 17.2) * mm});
            skLineSegment(sketch, "E986", {"start": v(55.32, 17.2) * mm, "end": v(56.13, 22.19) * mm});
            skLineSegment(sketch, "E987", {"start": v(55.86, 17.11) * mm, "end": v(55.2, 15.66) * mm});
            skLineSegment(sketch, "E988", {"start": v(55.2, 15.66) * mm, "end": v(54.2, 14.6) * mm});
            skLineSegment(sketch, "E989", {"start": v(56.74, 15.5) * mm, "end": v(56.74, 14.66) * mm});
            skLineSegment(sketch, "E990", {"start": v(56.74, 14.66) * mm, "end": v(58.52, 14.09) * mm});
            skLineSegment(sketch, "E991", {"start": v(58.52, 14.09) * mm, "end": v(61.33, 14.09) * mm});
            skLineSegment(sketch, "E992", {"start": v(56.18, 13.29) * mm, "end": v(55.76, 13.92) * mm});
            skLineSegment(sketch, "E993", {"start": v(55.76, 13.92) * mm, "end": v(58.14, 13.2) * mm});
            skLineSegment(sketch, "E994", {"start": v(58.14, 13.2) * mm, "end": v(59.62, 11.56) * mm});
            skLineSegment(sketch, "E995", {"start": v(58.14, 13.2) * mm, "end": v(58.62, 13.63) * mm});
            skLineSegment(sketch, "E996", {"start": v(-54.3, 15.52) * mm, "end": v(-45.9, 15.26) * mm});
            skLineSegment(sketch, "E997", {"start": v(-22.29, 40.86) * mm, "end": v(-13.93, 40.7) * mm});
            skLineSegment(sketch, "E998.bottom", {"start": v(-71.08, 66.4) * mm, "end": v(67.5, 66.4) * mm});
            skLineSegment(sketch, "E998.top", {"start": v(-71.23, -11) * mm, "end": v(67.13, -11) * mm});
            skLineSegment(sketch, "E998.left", {"start": v(-79.02, 62.55) * mm, "end": v(-79.02, -6.86) * mm});
            skLineSegment(sketch, "E998.right", {"start": v(70.98, 62.48) * mm, "end": v(70.98, -6.81) * mm});
            skLineSegment(sketch, "E999", {"start": v(-58.48, 32.14) * mm, "end": v(-54.33, 28.76) * mm});
            skLineSegment(sketch, "E1000", {"start": v(-54.33, 28.76) * mm, "end": v(-42.5, 26.75) * mm});
            skArc(sketch, "E1001", {"start": v(65.88, -11) * mm, "mid": v(69.35, -10.03) * mm, "end": v(70.98, -6.81) * mm});
            skArc(sketch, "E1002", {"start": v(70.98, 61.58) * mm, "mid": v(70.16, 64.65) * mm, "end": v(67.5, 66.4) * mm});
            skArc(sketch, "E1003", {"start": v(-79.02, -6.86) * mm, "mid": v(-75.64, -9.9) * mm, "end": v(-71.23, -11) * mm});
            skArc(sketch, "E1004", {"start": v(-71.08, 66.4) * mm, "mid": v(-75.5, 65.4) * mm, "end": v(-79.02, 62.55) * mm});
            skSolve(sketch);
        }
        {
            var Q0;
            Q0 = qSketchRegion(id + "F0", true);
            extrude(context, id + "F1", {"entities" : qUnion([Q0]), "depth" : 4.2 * mm, "offsetDistance" : 25 * mm});
        }
    });
